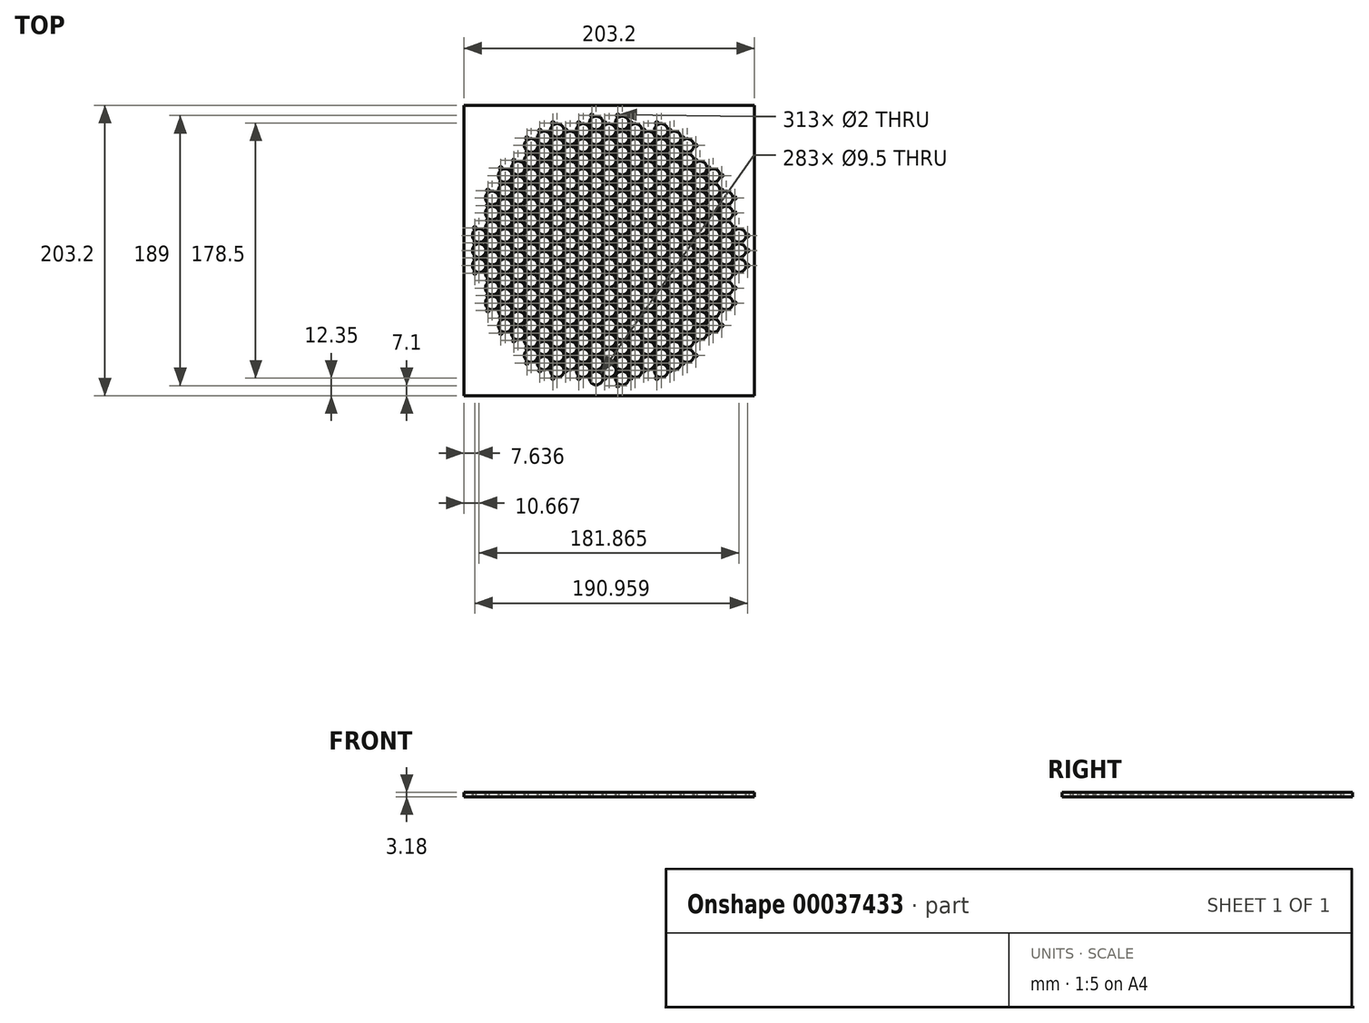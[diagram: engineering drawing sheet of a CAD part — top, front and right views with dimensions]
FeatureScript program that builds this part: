
annotation { "Feature Type Name" : "Feature", "Feature Type Description" : "" }
export const myFeature = defineFeature(function(context is Context, id is Id, definition is map)
    precondition{}
    {
        {
            var Q0;
            Q0=qCreatedBy(makeId("Top.planeOp"),FACE);
            var sketch = newSketch(context, id + "F0", { "sketchPlane" : qUnion([Q0])});
            skLineSegment(sketch, "E0.rect.bottom", {"start": v(101.6, 101.6) * mm, "end": v(-101.6, 101.6) * mm});
            skLineSegment(sketch, "E0.rect.top", {"start": v(101.6, -101.6) * mm, "end": v(-101.6, -101.6) * mm});
            skLineSegment(sketch, "E0.rect.left", {"start": v(101.6, 101.6) * mm, "end": v(101.6, -101.6) * mm});
            skLineSegment(sketch, "E0.rect.right", {"start": v(-101.6, 101.6) * mm, "end": v(-101.6, -101.6) * mm});
            skPoint(sketch, "E0.rect.middle", {"position": v(0, 0) * mm});
            skSolve(sketch);
        }
        {
            var Q0;
            Q0=qSketchRegion(id+"F0",true);
            extrude(context, id + "F1", {"entities" : qUnion([Q0]), "oppositeDirection" : true, "depth" : 3.17 * mm});
        }
        {
            var Q0;
            Q0=qCreatedBy(makeId("Top.planeOp"),FACE);
            var sketch = newSketch(context, id + "F2", { "sketchPlane" : qUnion([Q0])});
            skCircle(sketch, "E1", {"center": v(0, 0) * mm, "radius": 4.75 * mm});
            skCircle(sketch, "E2", {"center": v(0, 10.5) * mm, "radius": 4.75 * mm});
            skCircle(sketch, "E3", {"center": v(0, 21) * mm, "radius": 4.75 * mm});
            skCircle(sketch, "E4", {"center": v(0, 31.5) * mm, "radius": 4.75 * mm});
            skCircle(sketch, "E5", {"center": v(0, 42) * mm, "radius": 4.75 * mm});
            skCircle(sketch, "E6", {"center": v(0, 52.5) * mm, "radius": 4.75 * mm});
            skCircle(sketch, "E7", {"center": v(0, 63) * mm, "radius": 4.75 * mm});
            skCircle(sketch, "E8", {"center": v(0, 73.5) * mm, "radius": 4.75 * mm});
            skCircle(sketch, "E9", {"center": v(0, 84) * mm, "radius": 4.75 * mm});
            skCircle(sketch, "E10", {"center": v(0, -10.5) * mm, "radius": 4.75 * mm});
            skCircle(sketch, "E11", {"center": v(0, -21) * mm, "radius": 4.75 * mm});
            skCircle(sketch, "E12", {"center": v(0, -31.5) * mm, "radius": 4.75 * mm});
            skCircle(sketch, "E13", {"center": v(0, -42) * mm, "radius": 4.75 * mm});
            skCircle(sketch, "E14", {"center": v(0, -52.5) * mm, "radius": 4.75 * mm});
            skCircle(sketch, "E15", {"center": v(0, -63) * mm, "radius": 4.75 * mm});
            skCircle(sketch, "E16", {"center": v(0, -73.5) * mm, "radius": 4.75 * mm});
            skCircle(sketch, "E17", {"center": v(0, -84) * mm, "radius": 4.75 * mm});
            skLineSegment(sketch, "E18", {"start": v(0, 0) * mm, "end": v(9.1, 5.25) * mm, "construction": true});
            skCircle(sketch, "E19", {"center": v(9.1, -5.25) * mm, "radius": 4.75 * mm});
            skCircle(sketch, "E20", {"center": v(9.1, 26.25) * mm, "radius": 4.75 * mm});
            skCircle(sketch, "E21", {"center": v(9.1, 5.25) * mm, "radius": 4.75 * mm});
            skCircle(sketch, "E22", {"center": v(9.1, -47.25) * mm, "radius": 4.75 * mm});
            skCircle(sketch, "E23", {"center": v(9.1, 68.25) * mm, "radius": 4.75 * mm});
            skCircle(sketch, "E24", {"center": v(9.1, -36.75) * mm, "radius": 4.75 * mm});
            skCircle(sketch, "E25", {"center": v(9.1, -15.75) * mm, "radius": 4.75 * mm});
            skCircle(sketch, "E26", {"center": v(9.1, -78.75) * mm, "radius": 4.75 * mm});
            skCircle(sketch, "E27", {"center": v(9.1, -57.75) * mm, "radius": 4.75 * mm});
            skCircle(sketch, "E28", {"center": v(9.1, 89.25) * mm, "radius": 4.75 * mm});
            skCircle(sketch, "E29", {"center": v(9.1, 57.75) * mm, "radius": 4.75 * mm});
            skCircle(sketch, "E30", {"center": v(9.1, -68.25) * mm, "radius": 4.75 * mm});
            skCircle(sketch, "E31", {"center": v(9.1, 15.75) * mm, "radius": 4.75 * mm});
            skCircle(sketch, "E32", {"center": v(9.1, 47.25) * mm, "radius": 4.75 * mm});
            skCircle(sketch, "E33", {"center": v(9.1, 36.75) * mm, "radius": 4.75 * mm});
            skCircle(sketch, "E34", {"center": v(9.1, 78.75) * mm, "radius": 4.75 * mm});
            skCircle(sketch, "E35", {"center": v(9.1, -26.25) * mm, "radius": 4.75 * mm});
            skCircle(sketch, "E36", {"center": v(9.1, -89.25) * mm, "radius": 4.75 * mm});
            skCircle(sketch, "E37.1.0.0", {"center": v(18.19, 10.5) * mm, "radius": 4.75 * mm});
            skCircle(sketch, "E37.1.0.1", {"center": v(27.28, -47.25) * mm, "radius": 4.75 * mm});
            skCircle(sketch, "E37.1.0.2", {"center": v(27.28, 78.75) * mm, "radius": 4.75 * mm});
            skCircle(sketch, "E37.1.0.3", {"center": v(27.28, 57.75) * mm, "radius": 4.75 * mm});
            skCircle(sketch, "E37.1.0.4", {"center": v(18.19, -84) * mm, "radius": 4.75 * mm});
            skCircle(sketch, "E37.1.0.5", {"center": v(18.19, 52.5) * mm, "radius": 4.75 * mm});
            skCircle(sketch, "E37.1.0.6", {"center": v(27.28, 26.25) * mm, "radius": 4.75 * mm});
            skCircle(sketch, "E37.1.0.7", {"center": v(18.19, 73.5) * mm, "radius": 4.75 * mm});
            skCircle(sketch, "E37.1.0.8", {"center": v(18.19, -42) * mm, "radius": 4.75 * mm});
            skCircle(sketch, "E37.1.0.9", {"center": v(18.19, -21) * mm, "radius": 4.75 * mm});
            skCircle(sketch, "E37.1.0.10", {"center": v(18.19, -31.5) * mm, "radius": 4.75 * mm});
            skCircle(sketch, "E37.1.0.11", {"center": v(27.28, 47.25) * mm, "radius": 4.75 * mm});
            skCircle(sketch, "E37.1.0.12", {"center": v(27.28, 68.25) * mm, "radius": 4.75 * mm});
            skCircle(sketch, "E37.1.0.14", {"center": v(18.19, 31.5) * mm, "radius": 4.75 * mm});
            skCircle(sketch, "E37.1.0.15", {"center": v(18.19, 63) * mm, "radius": 4.75 * mm});
            skCircle(sketch, "E37.1.0.16", {"center": v(27.28, -26.25) * mm, "radius": 4.75 * mm});
            skCircle(sketch, "E37.1.0.17", {"center": v(18.19, -63) * mm, "radius": 4.75 * mm});
            skCircle(sketch, "E37.1.0.18", {"center": v(18.19, -10.5) * mm, "radius": 4.75 * mm});
            skCircle(sketch, "E37.1.0.19", {"center": v(27.28, 36.75) * mm, "radius": 4.75 * mm});
            skCircle(sketch, "E37.1.0.20", {"center": v(18.19, -73.5) * mm, "radius": 4.75 * mm});
            skCircle(sketch, "E37.1.0.21", {"center": v(27.28, -5.25) * mm, "radius": 4.75 * mm});
            skCircle(sketch, "E37.1.0.22", {"center": v(18.19, 21) * mm, "radius": 4.75 * mm});
            skCircle(sketch, "E37.1.0.23", {"center": v(27.28, -57.75) * mm, "radius": 4.75 * mm});
            skCircle(sketch, "E37.1.0.24", {"center": v(18.19, 84) * mm, "radius": 4.75 * mm});
            skCircle(sketch, "E37.1.0.25", {"center": v(27.28, -15.75) * mm, "radius": 4.75 * mm});
            skCircle(sketch, "E37.1.0.26", {"center": v(18.19, 42) * mm, "radius": 4.75 * mm});
            skCircle(sketch, "E37.1.0.27", {"center": v(27.28, 15.75) * mm, "radius": 4.75 * mm});
            skCircle(sketch, "E37.1.0.28", {"center": v(27.28, -68.25) * mm, "radius": 4.75 * mm});
            skCircle(sketch, "E37.1.0.29", {"center": v(27.28, -36.75) * mm, "radius": 4.75 * mm});
            skCircle(sketch, "E37.1.0.31", {"center": v(18.19, 0) * mm, "radius": 4.75 * mm});
            skCircle(sketch, "E37.1.0.32", {"center": v(27.28, -78.75) * mm, "radius": 4.75 * mm});
            skCircle(sketch, "E37.1.0.33", {"center": v(18.19, -52.5) * mm, "radius": 4.75 * mm});
            skCircle(sketch, "E37.1.0.34", {"center": v(27.28, 5.25) * mm, "radius": 4.75 * mm});
            skCircle(sketch, "E37.2.0.0", {"center": v(36.37, 10.5) * mm, "radius": 4.75 * mm});
            skCircle(sketch, "E37.2.0.1", {"center": v(45.47, -47.25) * mm, "radius": 4.75 * mm});
            skCircle(sketch, "E37.2.0.2", {"center": v(45.47, 78.75) * mm, "radius": 4.75 * mm});
            skCircle(sketch, "E37.2.0.3", {"center": v(45.47, 57.75) * mm, "radius": 4.75 * mm});
            skCircle(sketch, "E37.2.0.4", {"center": v(36.37, -84) * mm, "radius": 4.75 * mm});
            skCircle(sketch, "E37.2.0.5", {"center": v(36.37, 52.5) * mm, "radius": 4.75 * mm});
            skCircle(sketch, "E37.2.0.6", {"center": v(45.47, 26.25) * mm, "radius": 4.75 * mm});
            skCircle(sketch, "E37.2.0.7", {"center": v(36.37, 73.5) * mm, "radius": 4.75 * mm});
            skCircle(sketch, "E37.2.0.8", {"center": v(36.37, -42) * mm, "radius": 4.75 * mm});
            skCircle(sketch, "E37.2.0.9", {"center": v(36.37, -21) * mm, "radius": 4.75 * mm});
            skCircle(sketch, "E37.2.0.10", {"center": v(36.37, -31.5) * mm, "radius": 4.75 * mm});
            skCircle(sketch, "E37.2.0.11", {"center": v(45.47, 47.25) * mm, "radius": 4.75 * mm});
            skCircle(sketch, "E37.2.0.12", {"center": v(45.47, 68.25) * mm, "radius": 4.75 * mm});
            skCircle(sketch, "E37.2.0.14", {"center": v(36.37, 31.5) * mm, "radius": 4.75 * mm});
            skCircle(sketch, "E37.2.0.15", {"center": v(36.37, 63) * mm, "radius": 4.75 * mm});
            skCircle(sketch, "E37.2.0.16", {"center": v(45.47, -26.25) * mm, "radius": 4.75 * mm});
            skCircle(sketch, "E37.2.0.17", {"center": v(36.37, -63) * mm, "radius": 4.75 * mm});
            skCircle(sketch, "E37.2.0.18", {"center": v(36.37, -10.5) * mm, "radius": 4.75 * mm});
            skCircle(sketch, "E37.2.0.19", {"center": v(45.47, 36.75) * mm, "radius": 4.75 * mm});
            skCircle(sketch, "E37.2.0.20", {"center": v(36.37, -73.5) * mm, "radius": 4.75 * mm});
            skCircle(sketch, "E37.2.0.21", {"center": v(45.47, -5.25) * mm, "radius": 4.75 * mm});
            skCircle(sketch, "E37.2.0.22", {"center": v(36.37, 21) * mm, "radius": 4.75 * mm});
            skCircle(sketch, "E37.2.0.23", {"center": v(45.47, -57.75) * mm, "radius": 4.75 * mm});
            skCircle(sketch, "E37.2.0.24", {"center": v(36.37, 84) * mm, "radius": 4.75 * mm});
            skCircle(sketch, "E37.2.0.25", {"center": v(45.47, -15.75) * mm, "radius": 4.75 * mm});
            skCircle(sketch, "E37.2.0.26", {"center": v(36.37, 42) * mm, "radius": 4.75 * mm});
            skCircle(sketch, "E37.2.0.27", {"center": v(45.47, 15.75) * mm, "radius": 4.75 * mm});
            skCircle(sketch, "E37.2.0.28", {"center": v(45.47, -68.25) * mm, "radius": 4.75 * mm});
            skCircle(sketch, "E37.2.0.29", {"center": v(45.47, -36.75) * mm, "radius": 4.75 * mm});
            skCircle(sketch, "E37.2.0.31", {"center": v(36.37, 0) * mm, "radius": 4.75 * mm});
            skCircle(sketch, "E37.2.0.32", {"center": v(45.47, -78.75) * mm, "radius": 4.75 * mm});
            skCircle(sketch, "E37.2.0.33", {"center": v(36.37, -52.5) * mm, "radius": 4.75 * mm});
            skCircle(sketch, "E37.2.0.34", {"center": v(45.47, 5.25) * mm, "radius": 4.75 * mm});
            skCircle(sketch, "E37.3.0.0", {"center": v(54.56, 10.5) * mm, "radius": 4.75 * mm});
            skCircle(sketch, "E37.3.0.1", {"center": v(63.65, -47.25) * mm, "radius": 4.75 * mm});
            skCircle(sketch, "E37.3.0.3", {"center": v(63.65, 57.75) * mm, "radius": 4.75 * mm});
            skCircle(sketch, "E37.3.0.5", {"center": v(54.56, 52.5) * mm, "radius": 4.75 * mm});
            skCircle(sketch, "E37.3.0.6", {"center": v(63.65, 26.25) * mm, "radius": 4.75 * mm});
            skCircle(sketch, "E37.3.0.7", {"center": v(54.56, 73.5) * mm, "radius": 4.75 * mm});
            skCircle(sketch, "E37.3.0.8", {"center": v(54.56, -42) * mm, "radius": 4.75 * mm});
            skCircle(sketch, "E37.3.0.9", {"center": v(54.56, -21) * mm, "radius": 4.75 * mm});
            skCircle(sketch, "E37.3.0.10", {"center": v(54.56, -31.5) * mm, "radius": 4.75 * mm});
            skCircle(sketch, "E37.3.0.11", {"center": v(63.65, 47.25) * mm, "radius": 4.75 * mm});
            skCircle(sketch, "E37.3.0.14", {"center": v(54.56, 31.5) * mm, "radius": 4.75 * mm});
            skCircle(sketch, "E37.3.0.15", {"center": v(54.56, 63) * mm, "radius": 4.75 * mm});
            skCircle(sketch, "E37.3.0.16", {"center": v(63.65, -26.25) * mm, "radius": 4.75 * mm});
            skCircle(sketch, "E37.3.0.17", {"center": v(54.56, -63) * mm, "radius": 4.75 * mm});
            skCircle(sketch, "E37.3.0.18", {"center": v(54.56, -10.5) * mm, "radius": 4.75 * mm});
            skCircle(sketch, "E37.3.0.19", {"center": v(63.65, 36.75) * mm, "radius": 4.75 * mm});
            skCircle(sketch, "E37.3.0.20", {"center": v(54.56, -73.5) * mm, "radius": 4.75 * mm});
            skCircle(sketch, "E37.3.0.21", {"center": v(63.65, -5.25) * mm, "radius": 4.75 * mm});
            skCircle(sketch, "E37.3.0.22", {"center": v(54.56, 21) * mm, "radius": 4.75 * mm});
            skCircle(sketch, "E37.3.0.23", {"center": v(63.65, -57.75) * mm, "radius": 4.75 * mm});
            skCircle(sketch, "E37.3.0.25", {"center": v(63.65, -15.75) * mm, "radius": 4.75 * mm});
            skCircle(sketch, "E37.3.0.26", {"center": v(54.56, 42) * mm, "radius": 4.75 * mm});
            skCircle(sketch, "E37.3.0.27", {"center": v(63.65, 15.75) * mm, "radius": 4.75 * mm});
            skCircle(sketch, "E37.3.0.29", {"center": v(63.65, -36.75) * mm, "radius": 4.75 * mm});
            skCircle(sketch, "E37.3.0.31", {"center": v(54.56, 0) * mm, "radius": 4.75 * mm});
            skCircle(sketch, "E37.3.0.33", {"center": v(54.56, -52.5) * mm, "radius": 4.75 * mm});
            skCircle(sketch, "E37.3.0.34", {"center": v(63.65, 5.25) * mm, "radius": 4.75 * mm});
            skCircle(sketch, "E37.4.0.0", {"center": v(72.75, 10.5) * mm, "radius": 4.75 * mm});
            skCircle(sketch, "E37.4.0.5", {"center": v(72.75, 52.5) * mm, "radius": 4.75 * mm});
            skCircle(sketch, "E37.4.0.6", {"center": v(81.84, 26.25) * mm, "radius": 4.75 * mm});
            skCircle(sketch, "E37.4.0.8", {"center": v(72.75, -42) * mm, "radius": 4.75 * mm});
            skCircle(sketch, "E37.4.0.9", {"center": v(72.75, -21) * mm, "radius": 4.75 * mm});
            skCircle(sketch, "E37.4.0.10", {"center": v(72.75, -31.5) * mm, "radius": 4.75 * mm});
            skCircle(sketch, "E37.4.0.14", {"center": v(72.75, 31.5) * mm, "radius": 4.75 * mm});
            skCircle(sketch, "E37.4.0.16", {"center": v(81.84, -26.25) * mm, "radius": 4.75 * mm});
            skCircle(sketch, "E37.4.0.18", {"center": v(72.75, -10.5) * mm, "radius": 4.75 * mm});
            skCircle(sketch, "E37.4.0.19", {"center": v(81.84, 36.75) * mm, "radius": 4.75 * mm});
            skCircle(sketch, "E37.4.0.21", {"center": v(81.84, -5.25) * mm, "radius": 4.75 * mm});
            skCircle(sketch, "E37.4.0.22", {"center": v(72.75, 21) * mm, "radius": 4.75 * mm});
            skCircle(sketch, "E37.4.0.25", {"center": v(81.84, -15.75) * mm, "radius": 4.75 * mm});
            skCircle(sketch, "E37.4.0.26", {"center": v(72.75, 42) * mm, "radius": 4.75 * mm});
            skCircle(sketch, "E37.4.0.27", {"center": v(81.84, 15.75) * mm, "radius": 4.75 * mm});
            skCircle(sketch, "E37.4.0.29", {"center": v(81.84, -36.75) * mm, "radius": 4.75 * mm});
            skCircle(sketch, "E37.4.0.31", {"center": v(72.75, 0) * mm, "radius": 4.75 * mm});
            skCircle(sketch, "E37.4.0.33", {"center": v(72.75, -52.5) * mm, "radius": 4.75 * mm});
            skCircle(sketch, "E37.4.0.34", {"center": v(81.84, 5.25) * mm, "radius": 4.75 * mm});
            skCircle(sketch, "E38.1.0.0", {"center": v(-9.1, 26.25) * mm, "radius": 4.75 * mm});
            skCircle(sketch, "E38.1.0.1", {"center": v(-9.1, 5.25) * mm, "radius": 4.75 * mm});
            skCircle(sketch, "E38.1.0.2", {"center": v(-9.1, -47.25) * mm, "radius": 4.75 * mm});
            skCircle(sketch, "E38.1.0.3", {"center": v(-18.19, 84) * mm, "radius": 4.75 * mm});
            skCircle(sketch, "E38.1.0.4", {"center": v(-18.19, 31.5) * mm, "radius": 4.75 * mm});
            skCircle(sketch, "E38.1.0.5", {"center": v(-9.1, 68.25) * mm, "radius": 4.75 * mm});
            skCircle(sketch, "E38.1.0.6", {"center": v(-18.19, 42) * mm, "radius": 4.75 * mm});
            skCircle(sketch, "E38.1.0.7", {"center": v(-18.19, -10.5) * mm, "radius": 4.75 * mm});
            skCircle(sketch, "E38.1.0.8", {"center": v(-9.1, -57.75) * mm, "radius": 4.75 * mm});
            skCircle(sketch, "E38.1.0.9", {"center": v(-18.19, -42) * mm, "radius": 4.75 * mm});
            skCircle(sketch, "E38.1.0.10", {"center": v(-18.19, 63) * mm, "radius": 4.75 * mm});
            skCircle(sketch, "E38.1.0.11", {"center": v(-18.19, 0) * mm, "radius": 4.75 * mm});
            skCircle(sketch, "E38.1.0.12", {"center": v(-18.19, -21) * mm, "radius": 4.75 * mm});
            skCircle(sketch, "E38.1.0.13", {"center": v(-18.19, 21) * mm, "radius": 4.75 * mm});
            skCircle(sketch, "E38.1.0.14", {"center": v(-18.19, -63) * mm, "radius": 4.75 * mm});
            skCircle(sketch, "E38.1.0.15", {"center": v(-18.19, 52.5) * mm, "radius": 4.75 * mm});
            skCircle(sketch, "E38.1.0.16", {"center": v(-9.1, -15.75) * mm, "radius": 4.75 * mm});
            skCircle(sketch, "E38.1.0.17", {"center": v(-18.19, -73.5) * mm, "radius": 4.75 * mm});
            skCircle(sketch, "E38.1.0.18", {"center": v(-18.19, 73.5) * mm, "radius": 4.75 * mm});
            skCircle(sketch, "E38.1.0.19", {"center": v(-18.19, -31.5) * mm, "radius": 4.75 * mm});
            skCircle(sketch, "E38.1.0.20", {"center": v(-18.19, -52.5) * mm, "radius": 4.75 * mm});
            skCircle(sketch, "E38.1.0.21", {"center": v(-9.1, 89.25) * mm, "radius": 4.75 * mm});
            skCircle(sketch, "E38.1.0.22", {"center": v(-9.1, -68.25) * mm, "radius": 4.75 * mm});
            skCircle(sketch, "E38.1.0.23", {"center": v(-9.1, 57.75) * mm, "radius": 4.75 * mm});
            skCircle(sketch, "E38.1.0.24", {"center": v(-9.1, 15.75) * mm, "radius": 4.75 * mm});
            skCircle(sketch, "E38.1.0.25", {"center": v(-9.1, 47.25) * mm, "radius": 4.75 * mm});
            skLineSegment(sketch, "E38.1.0.26", {"start": v(-18.19, 10.5) * mm, "end": v(0, 10.5) * mm, "construction": true});
            skCircle(sketch, "E38.1.0.27", {"center": v(-9.1, 36.75) * mm, "radius": 4.75 * mm});
            skCircle(sketch, "E38.1.0.28", {"center": v(-18.19, -84) * mm, "radius": 4.75 * mm});
            skCircle(sketch, "E38.1.0.29", {"center": v(-9.1, 78.75) * mm, "radius": 4.75 * mm});
            skCircle(sketch, "E38.1.0.30", {"center": v(-9.1, -26.25) * mm, "radius": 4.75 * mm});
            skCircle(sketch, "E38.1.0.31", {"center": v(-9.1, -5.25) * mm, "radius": 4.75 * mm});
            skCircle(sketch, "E38.1.0.32", {"center": v(-9.1, -89.25) * mm, "radius": 4.75 * mm});
            skCircle(sketch, "E38.1.0.33", {"center": v(-18.19, 10.5) * mm, "radius": 4.75 * mm});
            skCircle(sketch, "E38.1.0.34", {"center": v(-9.1, -36.75) * mm, "radius": 4.75 * mm});
            skCircle(sketch, "E38.1.0.35", {"center": v(-9.1, -78.75) * mm, "radius": 4.75 * mm});
            skLineSegment(sketch, "E38.1.0.36", {"start": v(-18.19, 0) * mm, "end": v(-9.1, 5.25) * mm, "construction": true});
            skCircle(sketch, "E38.2.0.0", {"center": v(-27.28, 26.25) * mm, "radius": 4.75 * mm});
            skCircle(sketch, "E38.2.0.1", {"center": v(-27.28, 5.25) * mm, "radius": 4.75 * mm});
            skCircle(sketch, "E38.2.0.2", {"center": v(-27.28, -47.25) * mm, "radius": 4.75 * mm});
            skCircle(sketch, "E38.2.0.3", {"center": v(-36.37, 84) * mm, "radius": 4.75 * mm});
            skCircle(sketch, "E38.2.0.4", {"center": v(-36.37, 31.5) * mm, "radius": 4.75 * mm});
            skCircle(sketch, "E38.2.0.5", {"center": v(-27.28, 68.25) * mm, "radius": 4.75 * mm});
            skCircle(sketch, "E38.2.0.6", {"center": v(-36.37, 42) * mm, "radius": 4.75 * mm});
            skCircle(sketch, "E38.2.0.7", {"center": v(-36.37, -10.5) * mm, "radius": 4.75 * mm});
            skCircle(sketch, "E38.2.0.8", {"center": v(-27.28, -57.75) * mm, "radius": 4.75 * mm});
            skCircle(sketch, "E38.2.0.9", {"center": v(-36.37, -42) * mm, "radius": 4.75 * mm});
            skCircle(sketch, "E38.2.0.10", {"center": v(-36.37, 63) * mm, "radius": 4.75 * mm});
            skCircle(sketch, "E38.2.0.11", {"center": v(-36.37, 0) * mm, "radius": 4.75 * mm});
            skCircle(sketch, "E38.2.0.12", {"center": v(-36.37, -21) * mm, "radius": 4.75 * mm});
            skCircle(sketch, "E38.2.0.13", {"center": v(-36.37, 21) * mm, "radius": 4.75 * mm});
            skCircle(sketch, "E38.2.0.14", {"center": v(-36.37, -63) * mm, "radius": 4.75 * mm});
            skCircle(sketch, "E38.2.0.15", {"center": v(-36.37, 52.5) * mm, "radius": 4.75 * mm});
            skCircle(sketch, "E38.2.0.16", {"center": v(-27.28, -15.75) * mm, "radius": 4.75 * mm});
            skCircle(sketch, "E38.2.0.17", {"center": v(-36.37, -73.5) * mm, "radius": 4.75 * mm});
            skCircle(sketch, "E38.2.0.18", {"center": v(-36.37, 73.5) * mm, "radius": 4.75 * mm});
            skCircle(sketch, "E38.2.0.19", {"center": v(-36.37, -31.5) * mm, "radius": 4.75 * mm});
            skCircle(sketch, "E38.2.0.20", {"center": v(-36.37, -52.5) * mm, "radius": 4.75 * mm});
            skCircle(sketch, "E38.2.0.22", {"center": v(-27.28, -68.25) * mm, "radius": 4.75 * mm});
            skCircle(sketch, "E38.2.0.23", {"center": v(-27.28, 57.75) * mm, "radius": 4.75 * mm});
            skCircle(sketch, "E38.2.0.24", {"center": v(-27.28, 15.75) * mm, "radius": 4.75 * mm});
            skCircle(sketch, "E38.2.0.25", {"center": v(-27.28, 47.25) * mm, "radius": 4.75 * mm});
            skLineSegment(sketch, "E38.2.0.26", {"start": v(-36.37, 10.5) * mm, "end": v(-18.19, 10.5) * mm, "construction": true});
            skCircle(sketch, "E38.2.0.27", {"center": v(-27.28, 36.75) * mm, "radius": 4.75 * mm});
            skCircle(sketch, "E38.2.0.28", {"center": v(-36.37, -84) * mm, "radius": 4.75 * mm});
            skCircle(sketch, "E38.2.0.29", {"center": v(-27.28, 78.75) * mm, "radius": 4.75 * mm});
            skCircle(sketch, "E38.2.0.30", {"center": v(-27.28, -26.25) * mm, "radius": 4.75 * mm});
            skCircle(sketch, "E38.2.0.31", {"center": v(-27.28, -5.25) * mm, "radius": 4.75 * mm});
            skCircle(sketch, "E38.2.0.33", {"center": v(-36.37, 10.5) * mm, "radius": 4.75 * mm});
            skCircle(sketch, "E38.2.0.34", {"center": v(-27.28, -36.75) * mm, "radius": 4.75 * mm});
            skCircle(sketch, "E38.2.0.35", {"center": v(-27.28, -78.75) * mm, "radius": 4.75 * mm});
            skLineSegment(sketch, "E38.2.0.36", {"start": v(-36.37, 0) * mm, "end": v(-27.28, 5.25) * mm, "construction": true});
            skCircle(sketch, "E38.3.0.0", {"center": v(-45.47, 26.25) * mm, "radius": 4.75 * mm});
            skCircle(sketch, "E38.3.0.1", {"center": v(-45.47, 5.25) * mm, "radius": 4.75 * mm});
            skCircle(sketch, "E38.3.0.2", {"center": v(-45.47, -47.25) * mm, "radius": 4.75 * mm});
            skCircle(sketch, "E38.3.0.4", {"center": v(-54.56, 31.5) * mm, "radius": 4.75 * mm});
            skCircle(sketch, "E38.3.0.5", {"center": v(-45.47, 68.25) * mm, "radius": 4.75 * mm});
            skCircle(sketch, "E38.3.0.6", {"center": v(-54.56, 42) * mm, "radius": 4.75 * mm});
            skCircle(sketch, "E38.3.0.7", {"center": v(-54.56, -10.5) * mm, "radius": 4.75 * mm});
            skCircle(sketch, "E38.3.0.8", {"center": v(-45.47, -57.75) * mm, "radius": 4.75 * mm});
            skCircle(sketch, "E38.3.0.9", {"center": v(-54.56, -42) * mm, "radius": 4.75 * mm});
            skCircle(sketch, "E38.3.0.10", {"center": v(-54.56, 63) * mm, "radius": 4.75 * mm});
            skCircle(sketch, "E38.3.0.11", {"center": v(-54.56, 0) * mm, "radius": 4.75 * mm});
            skCircle(sketch, "E38.3.0.12", {"center": v(-54.56, -21) * mm, "radius": 4.75 * mm});
            skCircle(sketch, "E38.3.0.13", {"center": v(-54.56, 21) * mm, "radius": 4.75 * mm});
            skCircle(sketch, "E38.3.0.14", {"center": v(-54.56, -63) * mm, "radius": 4.75 * mm});
            skCircle(sketch, "E38.3.0.15", {"center": v(-54.56, 52.5) * mm, "radius": 4.75 * mm});
            skCircle(sketch, "E38.3.0.16", {"center": v(-45.47, -15.75) * mm, "radius": 4.75 * mm});
            skCircle(sketch, "E38.3.0.17", {"center": v(-54.56, -73.5) * mm, "radius": 4.75 * mm});
            skCircle(sketch, "E38.3.0.18", {"center": v(-54.56, 73.5) * mm, "radius": 4.75 * mm});
            skCircle(sketch, "E38.3.0.19", {"center": v(-54.56, -31.5) * mm, "radius": 4.75 * mm});
            skCircle(sketch, "E38.3.0.20", {"center": v(-54.56, -52.5) * mm, "radius": 4.75 * mm});
            skCircle(sketch, "E38.3.0.22", {"center": v(-45.47, -68.25) * mm, "radius": 4.75 * mm});
            skCircle(sketch, "E38.3.0.23", {"center": v(-45.47, 57.75) * mm, "radius": 4.75 * mm});
            skCircle(sketch, "E38.3.0.24", {"center": v(-45.47, 15.75) * mm, "radius": 4.75 * mm});
            skCircle(sketch, "E38.3.0.25", {"center": v(-45.47, 47.25) * mm, "radius": 4.75 * mm});
            skLineSegment(sketch, "E38.3.0.26", {"start": v(-54.56, 10.5) * mm, "end": v(-36.37, 10.5) * mm, "construction": true});
            skCircle(sketch, "E38.3.0.27", {"center": v(-45.47, 36.75) * mm, "radius": 4.75 * mm});
            skCircle(sketch, "E38.3.0.29", {"center": v(-45.47, 78.75) * mm, "radius": 4.75 * mm});
            skCircle(sketch, "E38.3.0.30", {"center": v(-45.47, -26.25) * mm, "radius": 4.75 * mm});
            skCircle(sketch, "E38.3.0.31", {"center": v(-45.47, -5.25) * mm, "radius": 4.75 * mm});
            skCircle(sketch, "E38.3.0.33", {"center": v(-54.56, 10.5) * mm, "radius": 4.75 * mm});
            skCircle(sketch, "E38.3.0.34", {"center": v(-45.47, -36.75) * mm, "radius": 4.75 * mm});
            skCircle(sketch, "E38.3.0.35", {"center": v(-45.47, -78.75) * mm, "radius": 4.75 * mm});
            skLineSegment(sketch, "E38.3.0.36", {"start": v(-54.56, 0) * mm, "end": v(-45.47, 5.25) * mm, "construction": true});
            skCircle(sketch, "E38.4.0.0", {"center": v(-63.65, 26.25) * mm, "radius": 4.75 * mm});
            skCircle(sketch, "E38.4.0.1", {"center": v(-63.65, 5.25) * mm, "radius": 4.75 * mm});
            skCircle(sketch, "E38.4.0.2", {"center": v(-63.65, -47.25) * mm, "radius": 4.75 * mm});
            skCircle(sketch, "E38.4.0.4", {"center": v(-72.75, 31.5) * mm, "radius": 4.75 * mm});
            skCircle(sketch, "E38.4.0.6", {"center": v(-72.75, 42) * mm, "radius": 4.75 * mm});
            skCircle(sketch, "E38.4.0.7", {"center": v(-72.75, -10.5) * mm, "radius": 4.75 * mm});
            skCircle(sketch, "E38.4.0.8", {"center": v(-63.65, -57.75) * mm, "radius": 4.75 * mm});
            skCircle(sketch, "E38.4.0.9", {"center": v(-72.75, -42) * mm, "radius": 4.75 * mm});
            skCircle(sketch, "E38.4.0.11", {"center": v(-72.75, 0) * mm, "radius": 4.75 * mm});
            skCircle(sketch, "E38.4.0.12", {"center": v(-72.75, -21) * mm, "radius": 4.75 * mm});
            skCircle(sketch, "E38.4.0.13", {"center": v(-72.75, 21) * mm, "radius": 4.75 * mm});
            skCircle(sketch, "E38.4.0.15", {"center": v(-72.75, 52.5) * mm, "radius": 4.75 * mm});
            skCircle(sketch, "E38.4.0.16", {"center": v(-63.65, -15.75) * mm, "radius": 4.75 * mm});
            skCircle(sketch, "E38.4.0.19", {"center": v(-72.75, -31.5) * mm, "radius": 4.75 * mm});
            skCircle(sketch, "E38.4.0.20", {"center": v(-72.75, -52.5) * mm, "radius": 4.75 * mm});
            skCircle(sketch, "E38.4.0.23", {"center": v(-63.65, 57.75) * mm, "radius": 4.75 * mm});
            skCircle(sketch, "E38.4.0.24", {"center": v(-63.65, 15.75) * mm, "radius": 4.75 * mm});
            skCircle(sketch, "E38.4.0.25", {"center": v(-63.65, 47.25) * mm, "radius": 4.75 * mm});
            skLineSegment(sketch, "E38.4.0.26", {"start": v(-72.75, 10.5) * mm, "end": v(-54.56, 10.5) * mm, "construction": true});
            skCircle(sketch, "E38.4.0.27", {"center": v(-63.65, 36.75) * mm, "radius": 4.75 * mm});
            skCircle(sketch, "E38.4.0.30", {"center": v(-63.65, -26.25) * mm, "radius": 4.75 * mm});
            skCircle(sketch, "E38.4.0.31", {"center": v(-63.65, -5.25) * mm, "radius": 4.75 * mm});
            skCircle(sketch, "E38.4.0.33", {"center": v(-72.75, 10.5) * mm, "radius": 4.75 * mm});
            skCircle(sketch, "E38.4.0.34", {"center": v(-63.65, -36.75) * mm, "radius": 4.75 * mm});
            skLineSegment(sketch, "E38.4.0.36", {"start": v(-72.75, 0) * mm, "end": v(-63.65, 5.25) * mm, "construction": true});
            skCircle(sketch, "E39", {"center": v(0, 0) * mm, "radius": 100 * mm, "construction": true});
            skCircle(sketch, "E40.1.0.0", {"center": v(-81.84, -26.25) * mm, "radius": 4.75 * mm});
            skCircle(sketch, "E40.1.0.8", {"center": v(-81.84, -5.25) * mm, "radius": 4.75 * mm});
            skCircle(sketch, "E40.1.0.13", {"center": v(-90.93, 0) * mm, "radius": 4.75 * mm});
            skCircle(sketch, "E40.1.0.14", {"center": v(-81.84, 36.75) * mm, "radius": 4.75 * mm});
            skCircle(sketch, "E40.1.0.19", {"center": v(-81.84, -36.75) * mm, "radius": 4.75 * mm});
            skCircle(sketch, "E40.1.0.22", {"center": v(-81.84, 15.75) * mm, "radius": 4.75 * mm});
            skCircle(sketch, "E40.1.0.25", {"center": v(-90.93, 10.5) * mm, "radius": 4.75 * mm});
            skCircle(sketch, "E40.1.0.26", {"center": v(-81.84, 5.25) * mm, "radius": 4.75 * mm});
            skCircle(sketch, "E40.1.0.28", {"center": v(-90.93, -10.5) * mm, "radius": 4.75 * mm});
            skCircle(sketch, "E40.1.0.29", {"center": v(-81.84, -15.75) * mm, "radius": 4.75 * mm});
            skCircle(sketch, "E40.1.0.31", {"center": v(-81.84, 26.25) * mm, "radius": 4.75 * mm});
            skLineSegment(sketch, "E40.1.0.35", {"start": v(-90.93, 0) * mm, "end": v(-81.84, 5.25) * mm, "construction": true});
            skLineSegment(sketch, "E40.direction1", {"start": v(-63.65, -26.25) * mm, "end": v(-81.84, -26.25) * mm, "construction": true});
            skCircle(sketch, "E41.1.0.3", {"center": v(90.93, 10.5) * mm, "radius": 4.75 * mm});
            skCircle(sketch, "E41.1.0.13", {"center": v(90.93, -10.5) * mm, "radius": 4.75 * mm});
            skCircle(sketch, "E41.1.0.30", {"center": v(90.93, 0) * mm, "radius": 4.75 * mm});
            skSolve(sketch);
        }
        {
            var Q0;
            Q0=qCreatedBy(makeId("Top.planeOp"),FACE);
            var sketch = newSketch(context, id + "F3", { "sketchPlane" : qUnion([Q0])});
            skCircle(sketch, "E42", {"center": v(6.06, 0) * mm, "radius": 1 * mm});
            skCircle(sketch, "E43.1.0", {"center": v(-3.03, 5.25) * mm, "radius": 1 * mm});
            skCircle(sketch, "E43.2.0", {"center": v(-3.03, -5.25) * mm, "radius": 1 * mm});
            skPoint(sketch, "E43.center", {"position": v(0, 0) * mm});
            skCircle(sketch, "E44.1.0.0", {"center": v(15.16, 5.25) * mm, "radius": 1 * mm});
            skCircle(sketch, "E44.1.0.1", {"center": v(24.25, 0) * mm, "radius": 1 * mm});
            skCircle(sketch, "E44.1.0.2", {"center": v(15.16, -5.25) * mm, "radius": 1 * mm});
            skCircle(sketch, "E44.2.0.0", {"center": v(33.34, 5.25) * mm, "radius": 1 * mm});
            skCircle(sketch, "E44.2.0.1", {"center": v(42.44, 0) * mm, "radius": 1 * mm});
            skCircle(sketch, "E44.2.0.2", {"center": v(33.34, -5.25) * mm, "radius": 1 * mm});
            skCircle(sketch, "E44.3.0.0", {"center": v(51.53, 5.25) * mm, "radius": 1 * mm});
            skCircle(sketch, "E44.3.0.1", {"center": v(60.62, 0) * mm, "radius": 1 * mm});
            skCircle(sketch, "E44.3.0.2", {"center": v(51.53, -5.25) * mm, "radius": 1 * mm});
            skCircle(sketch, "E44.4.0.0", {"center": v(69.72, 5.25) * mm, "radius": 1 * mm});
            skCircle(sketch, "E44.4.0.1", {"center": v(78.8, 0) * mm, "radius": 1 * mm});
            skCircle(sketch, "E44.4.0.2", {"center": v(69.72, -5.25) * mm, "radius": 1 * mm});
            skCircle(sketch, "E44.5.0.0", {"center": v(87.9, 5.25) * mm, "radius": 1 * mm});
            skCircle(sketch, "E44.5.0.1", {"center": v(97, 0) * mm, "radius": 1 * mm});
            skCircle(sketch, "E44.5.0.2", {"center": v(87.9, -5.25) * mm, "radius": 1 * mm});
            skCircle(sketch, "E45.1.0.0", {"center": v(-12.12, 0) * mm, "radius": 1 * mm});
            skCircle(sketch, "E45.1.0.1", {"center": v(-21.22, -5.25) * mm, "radius": 1 * mm});
            skCircle(sketch, "E45.1.0.2", {"center": v(-21.22, 5.25) * mm, "radius": 1 * mm});
            skCircle(sketch, "E45.2.0.0", {"center": v(-30.31, 0) * mm, "radius": 1 * mm});
            skCircle(sketch, "E45.2.0.1", {"center": v(-39.4, -5.25) * mm, "radius": 1 * mm});
            skCircle(sketch, "E45.2.0.2", {"center": v(-39.4, 5.25) * mm, "radius": 1 * mm});
            skCircle(sketch, "E45.3.0.0", {"center": v(-48.5, 0) * mm, "radius": 1 * mm});
            skCircle(sketch, "E45.3.0.1", {"center": v(-57.6, -5.25) * mm, "radius": 1 * mm});
            skCircle(sketch, "E45.3.0.2", {"center": v(-57.6, 5.25) * mm, "radius": 1 * mm});
            skCircle(sketch, "E45.4.0.0", {"center": v(-66.68, 0) * mm, "radius": 1 * mm});
            skCircle(sketch, "E45.4.0.1", {"center": v(-75.78, -5.25) * mm, "radius": 1 * mm});
            skCircle(sketch, "E45.4.0.2", {"center": v(-75.78, 5.25) * mm, "radius": 1 * mm});
            skCircle(sketch, "E45.5.0.0", {"center": v(-84.87, 0) * mm, "radius": 1 * mm});
            skCircle(sketch, "E45.5.0.1", {"center": v(-93.96, -5.25) * mm, "radius": 1 * mm});
            skCircle(sketch, "E45.5.0.2", {"center": v(-93.96, 5.25) * mm, "radius": 1 * mm});
            skPoint(sketch, "E46.0.1.1", {"position": v(0, 10.5) * mm});
            skCircle(sketch, "E46.0.1.6", {"center": v(-48.5, 10.5) * mm, "radius": 1 * mm});
            skCircle(sketch, "E46.0.1.8", {"center": v(51.53, 15.75) * mm, "radius": 1 * mm});
            skCircle(sketch, "E46.0.1.10", {"center": v(42.44, 10.5) * mm, "radius": 1 * mm});
            skCircle(sketch, "E46.0.1.11", {"center": v(33.34, 15.75) * mm, "radius": 1 * mm});
            skCircle(sketch, "E46.0.1.12", {"center": v(24.25, 10.5) * mm, "radius": 1 * mm});
            skCircle(sketch, "E46.0.1.13", {"center": v(-57.6, 15.75) * mm, "radius": 1 * mm});
            skCircle(sketch, "E46.0.1.15", {"center": v(-39.4, 15.75) * mm, "radius": 1 * mm});
            skCircle(sketch, "E46.0.1.17", {"center": v(87.9, 15.75) * mm, "radius": 1 * mm});
            skCircle(sketch, "E46.0.1.18", {"center": v(60.62, 10.5) * mm, "radius": 1 * mm});
            skCircle(sketch, "E46.0.1.19", {"center": v(-66.68, 10.5) * mm, "radius": 1 * mm});
            skCircle(sketch, "E46.0.1.20", {"center": v(-30.31, 10.5) * mm, "radius": 1 * mm});
            skCircle(sketch, "E46.0.1.21", {"center": v(-75.78, 15.75) * mm, "radius": 1 * mm});
            skCircle(sketch, "E46.0.1.23", {"center": v(-93.96, 15.75) * mm, "radius": 1 * mm});
            skCircle(sketch, "E46.0.1.27", {"center": v(97, 10.5) * mm, "radius": 1 * mm});
            skCircle(sketch, "E46.0.1.29", {"center": v(78.8, 10.5) * mm, "radius": 1 * mm});
            skCircle(sketch, "E46.0.1.30", {"center": v(69.72, 15.75) * mm, "radius": 1 * mm});
            skCircle(sketch, "E46.0.1.31", {"center": v(-84.87, 10.5) * mm, "radius": 1 * mm});
            skCircle(sketch, "E46.0.1.33", {"center": v(-21.22, 15.75) * mm, "radius": 1 * mm});
            skCircle(sketch, "E46.0.1.34", {"center": v(6.06, 10.5) * mm, "radius": 1 * mm});
            skCircle(sketch, "E46.0.1.35", {"center": v(-12.12, 10.5) * mm, "radius": 1 * mm});
            skCircle(sketch, "E46.0.1.36", {"center": v(15.16, 15.75) * mm, "radius": 1 * mm});
            skCircle(sketch, "E46.0.1.37", {"center": v(-3.03, 15.75) * mm, "radius": 1 * mm});
            skPoint(sketch, "E46.0.2.1", {"position": v(0, 21) * mm});
            skCircle(sketch, "E46.0.2.5", {"center": v(87.9, 15.75) * mm, "radius": 1 * mm});
            skCircle(sketch, "E46.0.2.6", {"center": v(-48.5, 21) * mm, "radius": 1 * mm});
            skCircle(sketch, "E46.0.2.7", {"center": v(-39.4, 15.75) * mm, "radius": 1 * mm});
            skCircle(sketch, "E46.0.2.8", {"center": v(51.53, 26.25) * mm, "radius": 1 * mm});
            skCircle(sketch, "E46.0.2.9", {"center": v(33.34, 15.75) * mm, "radius": 1 * mm});
            skCircle(sketch, "E46.0.2.10", {"center": v(42.44, 21) * mm, "radius": 1 * mm});
            skCircle(sketch, "E46.0.2.11", {"center": v(33.34, 26.25) * mm, "radius": 1 * mm});
            skCircle(sketch, "E46.0.2.12", {"center": v(24.25, 21) * mm, "radius": 1 * mm});
            skCircle(sketch, "E46.0.2.13", {"center": v(-57.6, 26.25) * mm, "radius": 1 * mm});
            skCircle(sketch, "E46.0.2.14", {"center": v(-75.78, 15.75) * mm, "radius": 1 * mm});
            skCircle(sketch, "E46.0.2.15", {"center": v(-39.4, 26.25) * mm, "radius": 1 * mm});
            skCircle(sketch, "E46.0.2.16", {"center": v(69.72, 15.75) * mm, "radius": 1 * mm});
            skCircle(sketch, "E46.0.2.17", {"center": v(87.9, 26.25) * mm, "radius": 1 * mm});
            skCircle(sketch, "E46.0.2.18", {"center": v(60.62, 21) * mm, "radius": 1 * mm});
            skCircle(sketch, "E46.0.2.19", {"center": v(-66.68, 21) * mm, "radius": 1 * mm});
            skCircle(sketch, "E46.0.2.20", {"center": v(-30.31, 21) * mm, "radius": 1 * mm});
            skCircle(sketch, "E46.0.2.21", {"center": v(-75.78, 26.25) * mm, "radius": 1 * mm});
            skCircle(sketch, "E46.0.2.22", {"center": v(-57.6, 15.75) * mm, "radius": 1 * mm});
            skCircle(sketch, "E46.0.2.24", {"center": v(-3.03, 15.75) * mm, "radius": 1 * mm});
            skCircle(sketch, "E46.0.2.25", {"center": v(15.16, 15.75) * mm, "radius": 1 * mm});
            skCircle(sketch, "E46.0.2.26", {"center": v(51.53, 15.75) * mm, "radius": 1 * mm});
            skCircle(sketch, "E46.0.2.28", {"center": v(-93.96, 15.75) * mm, "radius": 1 * mm});
            skCircle(sketch, "E46.0.2.29", {"center": v(78.8, 21) * mm, "radius": 1 * mm});
            skCircle(sketch, "E46.0.2.30", {"center": v(69.72, 26.25) * mm, "radius": 1 * mm});
            skCircle(sketch, "E46.0.2.31", {"center": v(-84.87, 21) * mm, "radius": 1 * mm});
            skCircle(sketch, "E46.0.2.32", {"center": v(-21.22, 15.75) * mm, "radius": 1 * mm});
            skCircle(sketch, "E46.0.2.33", {"center": v(-21.22, 26.25) * mm, "radius": 1 * mm});
            skCircle(sketch, "E46.0.2.34", {"center": v(6.06, 21) * mm, "radius": 1 * mm});
            skCircle(sketch, "E46.0.2.35", {"center": v(-12.12, 21) * mm, "radius": 1 * mm});
            skCircle(sketch, "E46.0.2.36", {"center": v(15.16, 26.25) * mm, "radius": 1 * mm});
            skCircle(sketch, "E46.0.2.37", {"center": v(-3.03, 26.25) * mm, "radius": 1 * mm});
            skPoint(sketch, "E46.0.3.1", {"position": v(0, 31.5) * mm});
            skCircle(sketch, "E46.0.3.5", {"center": v(87.9, 26.25) * mm, "radius": 1 * mm});
            skCircle(sketch, "E46.0.3.6", {"center": v(-48.5, 31.5) * mm, "radius": 1 * mm});
            skCircle(sketch, "E46.0.3.7", {"center": v(-39.4, 26.25) * mm, "radius": 1 * mm});
            skCircle(sketch, "E46.0.3.8", {"center": v(51.53, 36.75) * mm, "radius": 1 * mm});
            skCircle(sketch, "E46.0.3.9", {"center": v(33.34, 26.25) * mm, "radius": 1 * mm});
            skCircle(sketch, "E46.0.3.10", {"center": v(42.44, 31.5) * mm, "radius": 1 * mm});
            skCircle(sketch, "E46.0.3.11", {"center": v(33.34, 36.75) * mm, "radius": 1 * mm});
            skCircle(sketch, "E46.0.3.12", {"center": v(24.25, 31.5) * mm, "radius": 1 * mm});
            skCircle(sketch, "E46.0.3.13", {"center": v(-57.6, 36.75) * mm, "radius": 1 * mm});
            skCircle(sketch, "E46.0.3.14", {"center": v(-75.78, 26.25) * mm, "radius": 1 * mm});
            skCircle(sketch, "E46.0.3.15", {"center": v(-39.4, 36.75) * mm, "radius": 1 * mm});
            skCircle(sketch, "E46.0.3.16", {"center": v(69.72, 26.25) * mm, "radius": 1 * mm});
            skCircle(sketch, "E46.0.3.17", {"center": v(87.9, 36.75) * mm, "radius": 1 * mm});
            skCircle(sketch, "E46.0.3.18", {"center": v(60.62, 31.5) * mm, "radius": 1 * mm});
            skCircle(sketch, "E46.0.3.19", {"center": v(-66.68, 31.5) * mm, "radius": 1 * mm});
            skCircle(sketch, "E46.0.3.20", {"center": v(-30.31, 31.5) * mm, "radius": 1 * mm});
            skCircle(sketch, "E46.0.3.21", {"center": v(-75.78, 36.75) * mm, "radius": 1 * mm});
            skCircle(sketch, "E46.0.3.22", {"center": v(-57.6, 26.25) * mm, "radius": 1 * mm});
            skCircle(sketch, "E46.0.3.24", {"center": v(-3.03, 26.25) * mm, "radius": 1 * mm});
            skCircle(sketch, "E46.0.3.25", {"center": v(15.16, 26.25) * mm, "radius": 1 * mm});
            skCircle(sketch, "E46.0.3.26", {"center": v(51.53, 26.25) * mm, "radius": 1 * mm});
            skCircle(sketch, "E46.0.3.29", {"center": v(78.8, 31.5) * mm, "radius": 1 * mm});
            skCircle(sketch, "E46.0.3.30", {"center": v(69.72, 36.75) * mm, "radius": 1 * mm});
            skCircle(sketch, "E46.0.3.31", {"center": v(-84.87, 31.5) * mm, "radius": 1 * mm});
            skCircle(sketch, "E46.0.3.32", {"center": v(-21.22, 26.25) * mm, "radius": 1 * mm});
            skCircle(sketch, "E46.0.3.33", {"center": v(-21.22, 36.75) * mm, "radius": 1 * mm});
            skCircle(sketch, "E46.0.3.34", {"center": v(6.06, 31.5) * mm, "radius": 1 * mm});
            skCircle(sketch, "E46.0.3.35", {"center": v(-12.12, 31.5) * mm, "radius": 1 * mm});
            skCircle(sketch, "E46.0.3.36", {"center": v(15.16, 36.75) * mm, "radius": 1 * mm});
            skCircle(sketch, "E46.0.3.37", {"center": v(-3.03, 36.75) * mm, "radius": 1 * mm});
            skPoint(sketch, "E46.0.4.1", {"position": v(0, 42) * mm});
            skCircle(sketch, "E46.0.4.5", {"center": v(87.9, 36.75) * mm, "radius": 1 * mm});
            skCircle(sketch, "E46.0.4.6", {"center": v(-48.5, 42) * mm, "radius": 1 * mm});
            skCircle(sketch, "E46.0.4.7", {"center": v(-39.4, 36.75) * mm, "radius": 1 * mm});
            skCircle(sketch, "E46.0.4.8", {"center": v(51.53, 47.25) * mm, "radius": 1 * mm});
            skCircle(sketch, "E46.0.4.9", {"center": v(33.34, 36.75) * mm, "radius": 1 * mm});
            skCircle(sketch, "E46.0.4.10", {"center": v(42.44, 42) * mm, "radius": 1 * mm});
            skCircle(sketch, "E46.0.4.11", {"center": v(33.34, 47.25) * mm, "radius": 1 * mm});
            skCircle(sketch, "E46.0.4.12", {"center": v(24.25, 42) * mm, "radius": 1 * mm});
            skCircle(sketch, "E46.0.4.13", {"center": v(-57.6, 47.25) * mm, "radius": 1 * mm});
            skCircle(sketch, "E46.0.4.14", {"center": v(-75.78, 36.75) * mm, "radius": 1 * mm});
            skCircle(sketch, "E46.0.4.15", {"center": v(-39.4, 47.25) * mm, "radius": 1 * mm});
            skCircle(sketch, "E46.0.4.16", {"center": v(69.72, 36.75) * mm, "radius": 1 * mm});
            skCircle(sketch, "E46.0.4.18", {"center": v(60.62, 42) * mm, "radius": 1 * mm});
            skCircle(sketch, "E46.0.4.19", {"center": v(-66.68, 42) * mm, "radius": 1 * mm});
            skCircle(sketch, "E46.0.4.20", {"center": v(-30.31, 42) * mm, "radius": 1 * mm});
            skCircle(sketch, "E46.0.4.21", {"center": v(-75.78, 47.25) * mm, "radius": 1 * mm});
            skCircle(sketch, "E46.0.4.22", {"center": v(-57.6, 36.75) * mm, "radius": 1 * mm});
            skCircle(sketch, "E46.0.4.24", {"center": v(-3.03, 36.75) * mm, "radius": 1 * mm});
            skCircle(sketch, "E46.0.4.25", {"center": v(15.16, 36.75) * mm, "radius": 1 * mm});
            skCircle(sketch, "E46.0.4.26", {"center": v(51.53, 36.75) * mm, "radius": 1 * mm});
            skCircle(sketch, "E46.0.4.29", {"center": v(78.8, 42) * mm, "radius": 1 * mm});
            skCircle(sketch, "E46.0.4.30", {"center": v(69.72, 47.25) * mm, "radius": 1 * mm});
            skCircle(sketch, "E46.0.4.31", {"center": v(-84.87, 42) * mm, "radius": 1 * mm});
            skCircle(sketch, "E46.0.4.32", {"center": v(-21.22, 36.75) * mm, "radius": 1 * mm});
            skCircle(sketch, "E46.0.4.33", {"center": v(-21.22, 47.25) * mm, "radius": 1 * mm});
            skCircle(sketch, "E46.0.4.34", {"center": v(6.06, 42) * mm, "radius": 1 * mm});
            skCircle(sketch, "E46.0.4.35", {"center": v(-12.12, 42) * mm, "radius": 1 * mm});
            skCircle(sketch, "E46.0.4.36", {"center": v(15.16, 47.25) * mm, "radius": 1 * mm});
            skCircle(sketch, "E46.0.4.37", {"center": v(-3.03, 47.25) * mm, "radius": 1 * mm});
            skPoint(sketch, "E46.0.5.1", {"position": v(0, 52.5) * mm});
            skCircle(sketch, "E46.0.5.6", {"center": v(-48.5, 52.5) * mm, "radius": 1 * mm});
            skCircle(sketch, "E46.0.5.7", {"center": v(-39.4, 47.25) * mm, "radius": 1 * mm});
            skCircle(sketch, "E46.0.5.8", {"center": v(51.53, 57.75) * mm, "radius": 1 * mm});
            skCircle(sketch, "E46.0.5.9", {"center": v(33.34, 47.25) * mm, "radius": 1 * mm});
            skCircle(sketch, "E46.0.5.10", {"center": v(42.44, 52.5) * mm, "radius": 1 * mm});
            skCircle(sketch, "E46.0.5.11", {"center": v(33.34, 57.75) * mm, "radius": 1 * mm});
            skCircle(sketch, "E46.0.5.12", {"center": v(24.25, 52.5) * mm, "radius": 1 * mm});
            skCircle(sketch, "E46.0.5.13", {"center": v(-57.6, 57.75) * mm, "radius": 1 * mm});
            skCircle(sketch, "E46.0.5.14", {"center": v(-75.78, 47.25) * mm, "radius": 1 * mm});
            skCircle(sketch, "E46.0.5.15", {"center": v(-39.4, 57.75) * mm, "radius": 1 * mm});
            skCircle(sketch, "E46.0.5.16", {"center": v(69.72, 47.25) * mm, "radius": 1 * mm});
            skCircle(sketch, "E46.0.5.18", {"center": v(60.62, 52.5) * mm, "radius": 1 * mm});
            skCircle(sketch, "E46.0.5.19", {"center": v(-66.68, 52.5) * mm, "radius": 1 * mm});
            skCircle(sketch, "E46.0.5.20", {"center": v(-30.31, 52.5) * mm, "radius": 1 * mm});
            skCircle(sketch, "E46.0.5.21", {"center": v(-75.78, 57.75) * mm, "radius": 1 * mm});
            skCircle(sketch, "E46.0.5.22", {"center": v(-57.6, 47.25) * mm, "radius": 1 * mm});
            skCircle(sketch, "E46.0.5.24", {"center": v(-3.03, 47.25) * mm, "radius": 1 * mm});
            skCircle(sketch, "E46.0.5.25", {"center": v(15.16, 47.25) * mm, "radius": 1 * mm});
            skCircle(sketch, "E46.0.5.26", {"center": v(51.53, 47.25) * mm, "radius": 1 * mm});
            skCircle(sketch, "E46.0.5.29", {"center": v(78.8, 52.5) * mm, "radius": 1 * mm});
            skCircle(sketch, "E46.0.5.30", {"center": v(69.72, 57.75) * mm, "radius": 1 * mm});
            skCircle(sketch, "E46.0.5.32", {"center": v(-21.22, 47.25) * mm, "radius": 1 * mm});
            skCircle(sketch, "E46.0.5.33", {"center": v(-21.22, 57.75) * mm, "radius": 1 * mm});
            skCircle(sketch, "E46.0.5.34", {"center": v(6.06, 52.5) * mm, "radius": 1 * mm});
            skCircle(sketch, "E46.0.5.35", {"center": v(-12.12, 52.5) * mm, "radius": 1 * mm});
            skCircle(sketch, "E46.0.5.36", {"center": v(15.16, 57.75) * mm, "radius": 1 * mm});
            skCircle(sketch, "E46.0.5.37", {"center": v(-3.03, 57.75) * mm, "radius": 1 * mm});
            skPoint(sketch, "E46.0.6.1", {"position": v(0, 63) * mm});
            skCircle(sketch, "E46.0.6.6", {"center": v(-48.5, 63) * mm, "radius": 1 * mm});
            skCircle(sketch, "E46.0.6.7", {"center": v(-39.4, 57.75) * mm, "radius": 1 * mm});
            skCircle(sketch, "E46.0.6.8", {"center": v(51.53, 68.25) * mm, "radius": 1 * mm});
            skCircle(sketch, "E46.0.6.9", {"center": v(33.34, 57.75) * mm, "radius": 1 * mm});
            skCircle(sketch, "E46.0.6.10", {"center": v(42.44, 63) * mm, "radius": 1 * mm});
            skCircle(sketch, "E46.0.6.11", {"center": v(33.34, 68.25) * mm, "radius": 1 * mm});
            skCircle(sketch, "E46.0.6.12", {"center": v(24.25, 63) * mm, "radius": 1 * mm});
            skCircle(sketch, "E46.0.6.13", {"center": v(-57.6, 68.25) * mm, "radius": 1 * mm});
            skCircle(sketch, "E46.0.6.14", {"center": v(-75.78, 57.75) * mm, "radius": 1 * mm});
            skCircle(sketch, "E46.0.6.15", {"center": v(-39.4, 68.25) * mm, "radius": 1 * mm});
            skCircle(sketch, "E46.0.6.16", {"center": v(69.72, 57.75) * mm, "radius": 1 * mm});
            skCircle(sketch, "E46.0.6.18", {"center": v(60.62, 63) * mm, "radius": 1 * mm});
            skCircle(sketch, "E46.0.6.19", {"center": v(-66.68, 63) * mm, "radius": 1 * mm});
            skCircle(sketch, "E46.0.6.20", {"center": v(-30.31, 63) * mm, "radius": 1 * mm});
            skCircle(sketch, "E46.0.6.22", {"center": v(-57.6, 57.75) * mm, "radius": 1 * mm});
            skCircle(sketch, "E46.0.6.24", {"center": v(-3.03, 57.75) * mm, "radius": 1 * mm});
            skCircle(sketch, "E46.0.6.25", {"center": v(15.16, 57.75) * mm, "radius": 1 * mm});
            skCircle(sketch, "E46.0.6.26", {"center": v(51.53, 57.75) * mm, "radius": 1 * mm});
            skCircle(sketch, "E46.0.6.32", {"center": v(-21.22, 57.75) * mm, "radius": 1 * mm});
            skCircle(sketch, "E46.0.6.33", {"center": v(-21.22, 68.25) * mm, "radius": 1 * mm});
            skCircle(sketch, "E46.0.6.34", {"center": v(6.06, 63) * mm, "radius": 1 * mm});
            skCircle(sketch, "E46.0.6.35", {"center": v(-12.12, 63) * mm, "radius": 1 * mm});
            skCircle(sketch, "E46.0.6.36", {"center": v(15.16, 68.25) * mm, "radius": 1 * mm});
            skCircle(sketch, "E46.0.6.37", {"center": v(-3.03, 68.25) * mm, "radius": 1 * mm});
            skPoint(sketch, "E46.0.7.1", {"position": v(0, 73.5) * mm});
            skCircle(sketch, "E46.0.7.6", {"center": v(-48.5, 73.5) * mm, "radius": 1 * mm});
            skCircle(sketch, "E46.0.7.7", {"center": v(-39.4, 68.25) * mm, "radius": 1 * mm});
            skCircle(sketch, "E46.0.7.8", {"center": v(51.53, 78.75) * mm, "radius": 1 * mm});
            skCircle(sketch, "E46.0.7.9", {"center": v(33.34, 68.25) * mm, "radius": 1 * mm});
            skCircle(sketch, "E46.0.7.10", {"center": v(42.44, 73.5) * mm, "radius": 1 * mm});
            skCircle(sketch, "E46.0.7.11", {"center": v(33.34, 78.75) * mm, "radius": 1 * mm});
            skCircle(sketch, "E46.0.7.12", {"center": v(24.25, 73.5) * mm, "radius": 1 * mm});
            skCircle(sketch, "E46.0.7.13", {"center": v(-57.6, 78.75) * mm, "radius": 1 * mm});
            skCircle(sketch, "E46.0.7.15", {"center": v(-39.4, 78.75) * mm, "radius": 1 * mm});
            skCircle(sketch, "E46.0.7.18", {"center": v(60.62, 73.5) * mm, "radius": 1 * mm});
            skCircle(sketch, "E46.0.7.20", {"center": v(-30.31, 73.5) * mm, "radius": 1 * mm});
            skCircle(sketch, "E46.0.7.22", {"center": v(-57.6, 68.25) * mm, "radius": 1 * mm});
            skCircle(sketch, "E46.0.7.24", {"center": v(-3.03, 68.25) * mm, "radius": 1 * mm});
            skCircle(sketch, "E46.0.7.25", {"center": v(15.16, 68.25) * mm, "radius": 1 * mm});
            skCircle(sketch, "E46.0.7.26", {"center": v(51.53, 68.25) * mm, "radius": 1 * mm});
            skCircle(sketch, "E46.0.7.32", {"center": v(-21.22, 68.25) * mm, "radius": 1 * mm});
            skCircle(sketch, "E46.0.7.33", {"center": v(-21.22, 78.75) * mm, "radius": 1 * mm});
            skCircle(sketch, "E46.0.7.34", {"center": v(6.06, 73.5) * mm, "radius": 1 * mm});
            skCircle(sketch, "E46.0.7.35", {"center": v(-12.12, 73.5) * mm, "radius": 1 * mm});
            skCircle(sketch, "E46.0.7.36", {"center": v(15.16, 78.75) * mm, "radius": 1 * mm});
            skCircle(sketch, "E46.0.7.37", {"center": v(-3.03, 78.75) * mm, "radius": 1 * mm});
            skPoint(sketch, "E46.0.8.1", {"position": v(0, 84) * mm});
            skCircle(sketch, "E46.0.8.6", {"center": v(-48.5, 84) * mm, "radius": 1 * mm});
            skCircle(sketch, "E46.0.8.7", {"center": v(-39.4, 78.75) * mm, "radius": 1 * mm});
            skCircle(sketch, "E46.0.8.9", {"center": v(33.34, 78.75) * mm, "radius": 1 * mm});
            skCircle(sketch, "E46.0.8.10", {"center": v(42.44, 84) * mm, "radius": 1 * mm});
            skCircle(sketch, "E46.0.8.11", {"center": v(33.34, 89.25) * mm, "radius": 1 * mm});
            skCircle(sketch, "E46.0.8.12", {"center": v(24.25, 84) * mm, "radius": 1 * mm});
            skCircle(sketch, "E46.0.8.15", {"center": v(-39.4, 89.25) * mm, "radius": 1 * mm});
            skCircle(sketch, "E46.0.8.20", {"center": v(-30.31, 84) * mm, "radius": 1 * mm});
            skCircle(sketch, "E46.0.8.22", {"center": v(-57.6, 78.75) * mm, "radius": 1 * mm});
            skCircle(sketch, "E46.0.8.24", {"center": v(-3.03, 78.75) * mm, "radius": 1 * mm});
            skCircle(sketch, "E46.0.8.25", {"center": v(15.16, 78.75) * mm, "radius": 1 * mm});
            skCircle(sketch, "E46.0.8.26", {"center": v(51.53, 78.75) * mm, "radius": 1 * mm});
            skCircle(sketch, "E46.0.8.32", {"center": v(-21.22, 78.75) * mm, "radius": 1 * mm});
            skCircle(sketch, "E46.0.8.33", {"center": v(-21.22, 89.25) * mm, "radius": 1 * mm});
            skCircle(sketch, "E46.0.8.34", {"center": v(6.06, 84) * mm, "radius": 1 * mm});
            skCircle(sketch, "E46.0.8.35", {"center": v(-12.12, 84) * mm, "radius": 1 * mm});
            skCircle(sketch, "E46.0.8.36", {"center": v(15.16, 89.25) * mm, "radius": 1 * mm});
            skCircle(sketch, "E46.0.8.37", {"center": v(-3.03, 89.25) * mm, "radius": 1 * mm});
            skCircle(sketch, "E46.0.9.7", {"center": v(-39.4, 89.25) * mm, "radius": 1 * mm});
            skCircle(sketch, "E46.0.9.9", {"center": v(33.34, 89.25) * mm, "radius": 1 * mm});
            skCircle(sketch, "E46.0.9.24", {"center": v(-3.03, 89.25) * mm, "radius": 1 * mm});
            skCircle(sketch, "E46.0.9.25", {"center": v(15.16, 89.25) * mm, "radius": 1 * mm});
            skCircle(sketch, "E46.0.9.32", {"center": v(-21.22, 89.25) * mm, "radius": 1 * mm});
            skCircle(sketch, "E46.0.9.34", {"center": v(6.06, 94.5) * mm, "radius": 1 * mm});
            skCircle(sketch, "E46.0.9.35", {"center": v(-12.12, 94.5) * mm, "radius": 1 * mm});
            skPoint(sketch, "E47.0.1.0", {"position": v(0, -10.5) * mm});
            skCircle(sketch, "E47.0.1.1", {"center": v(33.34, -15.75) * mm, "radius": 1 * mm});
            skCircle(sketch, "E47.0.1.2", {"center": v(42.44, -10.5) * mm, "radius": 1 * mm});
            skCircle(sketch, "E47.0.1.3", {"center": v(15.16, -15.75) * mm, "radius": 1 * mm});
            skCircle(sketch, "E47.0.1.4", {"center": v(-3.03, -15.75) * mm, "radius": 1 * mm});
            skCircle(sketch, "E47.0.1.5", {"center": v(51.53, -15.75) * mm, "radius": 1 * mm});
            skCircle(sketch, "E47.0.1.6", {"center": v(60.62, -10.5) * mm, "radius": 1 * mm});
            skCircle(sketch, "E47.0.1.7", {"center": v(-48.5, -10.5) * mm, "radius": 1 * mm});
            skCircle(sketch, "E47.0.1.8", {"center": v(-39.4, -15.75) * mm, "radius": 1 * mm});
            skCircle(sketch, "E47.0.1.9", {"center": v(-30.31, -10.5) * mm, "radius": 1 * mm});
            skCircle(sketch, "E47.0.1.10", {"center": v(-21.22, -15.75) * mm, "radius": 1 * mm});
            skCircle(sketch, "E47.0.1.11", {"center": v(87.9, -15.75) * mm, "radius": 1 * mm});
            skCircle(sketch, "E47.0.1.12", {"center": v(78.8, -10.5) * mm, "radius": 1 * mm});
            skCircle(sketch, "E47.0.1.13", {"center": v(-93.96, -15.75) * mm, "radius": 1 * mm});
            skCircle(sketch, "E47.0.1.14", {"center": v(97, -10.5) * mm, "radius": 1 * mm});
            skCircle(sketch, "E47.0.1.15", {"center": v(-84.87, -10.5) * mm, "radius": 1 * mm});
            skCircle(sketch, "E47.0.1.16", {"center": v(-57.6, -15.75) * mm, "radius": 1 * mm});
            skCircle(sketch, "E47.0.1.17", {"center": v(-75.78, -15.75) * mm, "radius": 1 * mm});
            skCircle(sketch, "E47.0.1.18", {"center": v(-66.68, -10.5) * mm, "radius": 1 * mm});
            skCircle(sketch, "E47.0.1.19", {"center": v(69.72, -15.75) * mm, "radius": 1 * mm});
            skCircle(sketch, "E47.0.1.22", {"center": v(24.25, -10.5) * mm, "radius": 1 * mm});
            skCircle(sketch, "E47.0.1.23", {"center": v(6.06, -10.5) * mm, "radius": 1 * mm});
            skCircle(sketch, "E47.0.1.29", {"center": v(-12.12, -10.5) * mm, "radius": 1 * mm});
            skPoint(sketch, "E47.0.2.0", {"position": v(0, -21) * mm});
            skCircle(sketch, "E47.0.2.1", {"center": v(33.34, -26.25) * mm, "radius": 1 * mm});
            skCircle(sketch, "E47.0.2.2", {"center": v(42.44, -21) * mm, "radius": 1 * mm});
            skCircle(sketch, "E47.0.2.3", {"center": v(15.16, -26.25) * mm, "radius": 1 * mm});
            skCircle(sketch, "E47.0.2.4", {"center": v(-3.03, -26.25) * mm, "radius": 1 * mm});
            skCircle(sketch, "E47.0.2.5", {"center": v(51.53, -26.25) * mm, "radius": 1 * mm});
            skCircle(sketch, "E47.0.2.6", {"center": v(60.62, -21) * mm, "radius": 1 * mm});
            skCircle(sketch, "E47.0.2.7", {"center": v(-48.5, -21) * mm, "radius": 1 * mm});
            skCircle(sketch, "E47.0.2.8", {"center": v(-39.4, -26.25) * mm, "radius": 1 * mm});
            skCircle(sketch, "E47.0.2.9", {"center": v(-30.31, -21) * mm, "radius": 1 * mm});
            skCircle(sketch, "E47.0.2.10", {"center": v(-21.22, -26.25) * mm, "radius": 1 * mm});
            skCircle(sketch, "E47.0.2.11", {"center": v(87.9, -26.25) * mm, "radius": 1 * mm});
            skCircle(sketch, "E47.0.2.12", {"center": v(78.8, -21) * mm, "radius": 1 * mm});
            skCircle(sketch, "E47.0.2.15", {"center": v(-84.87, -21) * mm, "radius": 1 * mm});
            skCircle(sketch, "E47.0.2.16", {"center": v(-57.6, -26.25) * mm, "radius": 1 * mm});
            skCircle(sketch, "E47.0.2.17", {"center": v(-75.78, -26.25) * mm, "radius": 1 * mm});
            skCircle(sketch, "E47.0.2.18", {"center": v(-66.68, -21) * mm, "radius": 1 * mm});
            skCircle(sketch, "E47.0.2.19", {"center": v(69.72, -26.25) * mm, "radius": 1 * mm});
            skCircle(sketch, "E47.0.2.20", {"center": v(51.53, -15.75) * mm, "radius": 1 * mm});
            skCircle(sketch, "E47.0.2.21", {"center": v(33.34, -15.75) * mm, "radius": 1 * mm});
            skCircle(sketch, "E47.0.2.22", {"center": v(24.25, -21) * mm, "radius": 1 * mm});
            skCircle(sketch, "E47.0.2.23", {"center": v(6.06, -21) * mm, "radius": 1 * mm});
            skCircle(sketch, "E47.0.2.24", {"center": v(69.72, -15.75) * mm, "radius": 1 * mm});
            skCircle(sketch, "E47.0.2.25", {"center": v(-39.4, -15.75) * mm, "radius": 1 * mm});
            skCircle(sketch, "E47.0.2.26", {"center": v(-57.6, -15.75) * mm, "radius": 1 * mm});
            skCircle(sketch, "E47.0.2.27", {"center": v(87.9, -15.75) * mm, "radius": 1 * mm});
            skCircle(sketch, "E47.0.2.28", {"center": v(-21.22, -15.75) * mm, "radius": 1 * mm});
            skCircle(sketch, "E47.0.2.29", {"center": v(-12.12, -21) * mm, "radius": 1 * mm});
            skCircle(sketch, "E47.0.2.30", {"center": v(-93.96, -15.75) * mm, "radius": 1 * mm});
            skCircle(sketch, "E47.0.2.31", {"center": v(-75.78, -15.75) * mm, "radius": 1 * mm});
            skCircle(sketch, "E47.0.2.32", {"center": v(15.16, -15.75) * mm, "radius": 1 * mm});
            skCircle(sketch, "E47.0.2.33", {"center": v(-3.03, -15.75) * mm, "radius": 1 * mm});
            skCircle(sketch, "E47.0.2.34", {"center": v(-39.4, -15.75) * mm, "radius": 1 * mm});
            skCircle(sketch, "E47.0.2.35", {"center": v(69.72, -15.75) * mm, "radius": 1 * mm});
            skCircle(sketch, "E47.0.2.36", {"center": v(-21.22, -15.75) * mm, "radius": 1 * mm});
            skCircle(sketch, "E47.0.2.37", {"center": v(87.9, -15.75) * mm, "radius": 1 * mm});
            skCircle(sketch, "E47.0.2.38", {"center": v(51.53, -15.75) * mm, "radius": 1 * mm});
            skCircle(sketch, "E47.0.2.39", {"center": v(-57.6, -15.75) * mm, "radius": 1 * mm});
            skCircle(sketch, "E47.0.2.40", {"center": v(33.34, -15.75) * mm, "radius": 1 * mm});
            skCircle(sketch, "E47.0.2.41", {"center": v(-75.78, -15.75) * mm, "radius": 1 * mm});
            skCircle(sketch, "E47.0.2.42", {"center": v(-93.96, -15.75) * mm, "radius": 1 * mm});
            skCircle(sketch, "E47.0.2.43", {"center": v(15.16, -15.75) * mm, "radius": 1 * mm});
            skCircle(sketch, "E47.0.2.44", {"center": v(-3.03, -15.75) * mm, "radius": 1 * mm});
            skPoint(sketch, "E47.0.3.0", {"position": v(0, -31.5) * mm});
            skCircle(sketch, "E47.0.3.1", {"center": v(33.34, -36.75) * mm, "radius": 1 * mm});
            skCircle(sketch, "E47.0.3.2", {"center": v(42.44, -31.5) * mm, "radius": 1 * mm});
            skCircle(sketch, "E47.0.3.3", {"center": v(15.16, -36.75) * mm, "radius": 1 * mm});
            skCircle(sketch, "E47.0.3.4", {"center": v(-3.03, -36.75) * mm, "radius": 1 * mm});
            skCircle(sketch, "E47.0.3.5", {"center": v(51.53, -36.75) * mm, "radius": 1 * mm});
            skCircle(sketch, "E47.0.3.6", {"center": v(60.62, -31.5) * mm, "radius": 1 * mm});
            skCircle(sketch, "E47.0.3.7", {"center": v(-48.5, -31.5) * mm, "radius": 1 * mm});
            skCircle(sketch, "E47.0.3.8", {"center": v(-39.4, -36.75) * mm, "radius": 1 * mm});
            skCircle(sketch, "E47.0.3.9", {"center": v(-30.31, -31.5) * mm, "radius": 1 * mm});
            skCircle(sketch, "E47.0.3.10", {"center": v(-21.22, -36.75) * mm, "radius": 1 * mm});
            skCircle(sketch, "E47.0.3.11", {"center": v(87.9, -36.75) * mm, "radius": 1 * mm});
            skCircle(sketch, "E47.0.3.12", {"center": v(78.8, -31.5) * mm, "radius": 1 * mm});
            skCircle(sketch, "E47.0.3.15", {"center": v(-84.87, -31.5) * mm, "radius": 1 * mm});
            skCircle(sketch, "E47.0.3.16", {"center": v(-57.6, -36.75) * mm, "radius": 1 * mm});
            skCircle(sketch, "E47.0.3.17", {"center": v(-75.78, -36.75) * mm, "radius": 1 * mm});
            skCircle(sketch, "E47.0.3.18", {"center": v(-66.68, -31.5) * mm, "radius": 1 * mm});
            skCircle(sketch, "E47.0.3.19", {"center": v(69.72, -36.75) * mm, "radius": 1 * mm});
            skCircle(sketch, "E47.0.3.20", {"center": v(51.53, -26.25) * mm, "radius": 1 * mm});
            skCircle(sketch, "E47.0.3.21", {"center": v(33.34, -26.25) * mm, "radius": 1 * mm});
            skCircle(sketch, "E47.0.3.22", {"center": v(24.25, -31.5) * mm, "radius": 1 * mm});
            skCircle(sketch, "E47.0.3.23", {"center": v(6.06, -31.5) * mm, "radius": 1 * mm});
            skCircle(sketch, "E47.0.3.24", {"center": v(69.72, -26.25) * mm, "radius": 1 * mm});
            skCircle(sketch, "E47.0.3.25", {"center": v(-39.4, -26.25) * mm, "radius": 1 * mm});
            skCircle(sketch, "E47.0.3.26", {"center": v(-57.6, -26.25) * mm, "radius": 1 * mm});
            skCircle(sketch, "E47.0.3.27", {"center": v(87.9, -26.25) * mm, "radius": 1 * mm});
            skCircle(sketch, "E47.0.3.28", {"center": v(-21.22, -26.25) * mm, "radius": 1 * mm});
            skCircle(sketch, "E47.0.3.29", {"center": v(-12.12, -31.5) * mm, "radius": 1 * mm});
            skCircle(sketch, "E47.0.3.31", {"center": v(-75.78, -26.25) * mm, "radius": 1 * mm});
            skCircle(sketch, "E47.0.3.32", {"center": v(15.16, -26.25) * mm, "radius": 1 * mm});
            skCircle(sketch, "E47.0.3.33", {"center": v(-3.03, -26.25) * mm, "radius": 1 * mm});
            skCircle(sketch, "E47.0.3.34", {"center": v(-39.4, -26.25) * mm, "radius": 1 * mm});
            skCircle(sketch, "E47.0.3.35", {"center": v(69.72, -26.25) * mm, "radius": 1 * mm});
            skCircle(sketch, "E47.0.3.36", {"center": v(-21.22, -26.25) * mm, "radius": 1 * mm});
            skCircle(sketch, "E47.0.3.37", {"center": v(87.9, -26.25) * mm, "radius": 1 * mm});
            skCircle(sketch, "E47.0.3.38", {"center": v(51.53, -26.25) * mm, "radius": 1 * mm});
            skCircle(sketch, "E47.0.3.39", {"center": v(-57.6, -26.25) * mm, "radius": 1 * mm});
            skCircle(sketch, "E47.0.3.40", {"center": v(33.34, -26.25) * mm, "radius": 1 * mm});
            skCircle(sketch, "E47.0.3.41", {"center": v(-75.78, -26.25) * mm, "radius": 1 * mm});
            skCircle(sketch, "E47.0.3.43", {"center": v(15.16, -26.25) * mm, "radius": 1 * mm});
            skCircle(sketch, "E47.0.3.44", {"center": v(-3.03, -26.25) * mm, "radius": 1 * mm});
            skPoint(sketch, "E47.0.4.0", {"position": v(0, -42) * mm});
            skCircle(sketch, "E47.0.4.1", {"center": v(33.34, -47.25) * mm, "radius": 1 * mm});
            skCircle(sketch, "E47.0.4.2", {"center": v(42.44, -42) * mm, "radius": 1 * mm});
            skCircle(sketch, "E47.0.4.3", {"center": v(15.16, -47.25) * mm, "radius": 1 * mm});
            skCircle(sketch, "E47.0.4.4", {"center": v(-3.03, -47.25) * mm, "radius": 1 * mm});
            skCircle(sketch, "E47.0.4.5", {"center": v(51.53, -47.25) * mm, "radius": 1 * mm});
            skCircle(sketch, "E47.0.4.6", {"center": v(60.62, -42) * mm, "radius": 1 * mm});
            skCircle(sketch, "E47.0.4.7", {"center": v(-48.5, -42) * mm, "radius": 1 * mm});
            skCircle(sketch, "E47.0.4.8", {"center": v(-39.4, -47.25) * mm, "radius": 1 * mm});
            skCircle(sketch, "E47.0.4.9", {"center": v(-30.31, -42) * mm, "radius": 1 * mm});
            skCircle(sketch, "E47.0.4.10", {"center": v(-21.22, -47.25) * mm, "radius": 1 * mm});
            skCircle(sketch, "E47.0.4.12", {"center": v(78.8, -42) * mm, "radius": 1 * mm});
            skCircle(sketch, "E47.0.4.15", {"center": v(-84.87, -42) * mm, "radius": 1 * mm});
            skCircle(sketch, "E47.0.4.16", {"center": v(-57.6, -47.25) * mm, "radius": 1 * mm});
            skCircle(sketch, "E47.0.4.17", {"center": v(-75.78, -47.25) * mm, "radius": 1 * mm});
            skCircle(sketch, "E47.0.4.18", {"center": v(-66.68, -42) * mm, "radius": 1 * mm});
            skCircle(sketch, "E47.0.4.19", {"center": v(69.72, -47.25) * mm, "radius": 1 * mm});
            skCircle(sketch, "E47.0.4.20", {"center": v(51.53, -36.75) * mm, "radius": 1 * mm});
            skCircle(sketch, "E47.0.4.21", {"center": v(33.34, -36.75) * mm, "radius": 1 * mm});
            skCircle(sketch, "E47.0.4.22", {"center": v(24.25, -42) * mm, "radius": 1 * mm});
            skCircle(sketch, "E47.0.4.23", {"center": v(6.06, -42) * mm, "radius": 1 * mm});
            skCircle(sketch, "E47.0.4.24", {"center": v(69.72, -36.75) * mm, "radius": 1 * mm});
            skCircle(sketch, "E47.0.4.25", {"center": v(-39.4, -36.75) * mm, "radius": 1 * mm});
            skCircle(sketch, "E47.0.4.26", {"center": v(-57.6, -36.75) * mm, "radius": 1 * mm});
            skCircle(sketch, "E47.0.4.27", {"center": v(87.9, -36.75) * mm, "radius": 1 * mm});
            skCircle(sketch, "E47.0.4.28", {"center": v(-21.22, -36.75) * mm, "radius": 1 * mm});
            skCircle(sketch, "E47.0.4.29", {"center": v(-12.12, -42) * mm, "radius": 1 * mm});
            skCircle(sketch, "E47.0.4.31", {"center": v(-75.78, -36.75) * mm, "radius": 1 * mm});
            skCircle(sketch, "E47.0.4.32", {"center": v(15.16, -36.75) * mm, "radius": 1 * mm});
            skCircle(sketch, "E47.0.4.33", {"center": v(-3.03, -36.75) * mm, "radius": 1 * mm});
            skCircle(sketch, "E47.0.4.34", {"center": v(-39.4, -36.75) * mm, "radius": 1 * mm});
            skCircle(sketch, "E47.0.4.35", {"center": v(69.72, -36.75) * mm, "radius": 1 * mm});
            skCircle(sketch, "E47.0.4.36", {"center": v(-21.22, -36.75) * mm, "radius": 1 * mm});
            skCircle(sketch, "E47.0.4.37", {"center": v(87.9, -36.75) * mm, "radius": 1 * mm});
            skCircle(sketch, "E47.0.4.38", {"center": v(51.53, -36.75) * mm, "radius": 1 * mm});
            skCircle(sketch, "E47.0.4.39", {"center": v(-57.6, -36.75) * mm, "radius": 1 * mm});
            skCircle(sketch, "E47.0.4.40", {"center": v(33.34, -36.75) * mm, "radius": 1 * mm});
            skCircle(sketch, "E47.0.4.41", {"center": v(-75.78, -36.75) * mm, "radius": 1 * mm});
            skCircle(sketch, "E47.0.4.43", {"center": v(15.16, -36.75) * mm, "radius": 1 * mm});
            skCircle(sketch, "E47.0.4.44", {"center": v(-3.03, -36.75) * mm, "radius": 1 * mm});
            skPoint(sketch, "E47.0.5.0", {"position": v(0, -52.5) * mm});
            skCircle(sketch, "E47.0.5.1", {"center": v(33.34, -57.75) * mm, "radius": 1 * mm});
            skCircle(sketch, "E47.0.5.2", {"center": v(42.44, -52.5) * mm, "radius": 1 * mm});
            skCircle(sketch, "E47.0.5.3", {"center": v(15.16, -57.75) * mm, "radius": 1 * mm});
            skCircle(sketch, "E47.0.5.4", {"center": v(-3.03, -57.75) * mm, "radius": 1 * mm});
            skCircle(sketch, "E47.0.5.5", {"center": v(51.53, -57.75) * mm, "radius": 1 * mm});
            skCircle(sketch, "E47.0.5.6", {"center": v(60.62, -52.5) * mm, "radius": 1 * mm});
            skCircle(sketch, "E47.0.5.7", {"center": v(-48.5, -52.5) * mm, "radius": 1 * mm});
            skCircle(sketch, "E47.0.5.8", {"center": v(-39.4, -57.75) * mm, "radius": 1 * mm});
            skCircle(sketch, "E47.0.5.9", {"center": v(-30.31, -52.5) * mm, "radius": 1 * mm});
            skCircle(sketch, "E47.0.5.10", {"center": v(-21.22, -57.75) * mm, "radius": 1 * mm});
            skCircle(sketch, "E47.0.5.12", {"center": v(78.8, -52.5) * mm, "radius": 1 * mm});
            skCircle(sketch, "E47.0.5.16", {"center": v(-57.6, -57.75) * mm, "radius": 1 * mm});
            skCircle(sketch, "E47.0.5.17", {"center": v(-75.78, -57.75) * mm, "radius": 1 * mm});
            skCircle(sketch, "E47.0.5.18", {"center": v(-66.68, -52.5) * mm, "radius": 1 * mm});
            skCircle(sketch, "E47.0.5.19", {"center": v(69.72, -57.75) * mm, "radius": 1 * mm});
            skCircle(sketch, "E47.0.5.20", {"center": v(51.53, -47.25) * mm, "radius": 1 * mm});
            skCircle(sketch, "E47.0.5.21", {"center": v(33.34, -47.25) * mm, "radius": 1 * mm});
            skCircle(sketch, "E47.0.5.22", {"center": v(24.25, -52.5) * mm, "radius": 1 * mm});
            skCircle(sketch, "E47.0.5.23", {"center": v(6.06, -52.5) * mm, "radius": 1 * mm});
            skCircle(sketch, "E47.0.5.24", {"center": v(69.72, -47.25) * mm, "radius": 1 * mm});
            skCircle(sketch, "E47.0.5.25", {"center": v(-39.4, -47.25) * mm, "radius": 1 * mm});
            skCircle(sketch, "E47.0.5.26", {"center": v(-57.6, -47.25) * mm, "radius": 1 * mm});
            skCircle(sketch, "E47.0.5.28", {"center": v(-21.22, -47.25) * mm, "radius": 1 * mm});
            skCircle(sketch, "E47.0.5.29", {"center": v(-12.12, -52.5) * mm, "radius": 1 * mm});
            skCircle(sketch, "E47.0.5.31", {"center": v(-75.78, -47.25) * mm, "radius": 1 * mm});
            skCircle(sketch, "E47.0.5.32", {"center": v(15.16, -47.25) * mm, "radius": 1 * mm});
            skCircle(sketch, "E47.0.5.33", {"center": v(-3.03, -47.25) * mm, "radius": 1 * mm});
            skCircle(sketch, "E47.0.5.34", {"center": v(-39.4, -47.25) * mm, "radius": 1 * mm});
            skCircle(sketch, "E47.0.5.35", {"center": v(69.72, -47.25) * mm, "radius": 1 * mm});
            skCircle(sketch, "E47.0.5.36", {"center": v(-21.22, -47.25) * mm, "radius": 1 * mm});
            skCircle(sketch, "E47.0.5.38", {"center": v(51.53, -47.25) * mm, "radius": 1 * mm});
            skCircle(sketch, "E47.0.5.39", {"center": v(-57.6, -47.25) * mm, "radius": 1 * mm});
            skCircle(sketch, "E47.0.5.40", {"center": v(33.34, -47.25) * mm, "radius": 1 * mm});
            skCircle(sketch, "E47.0.5.41", {"center": v(-75.78, -47.25) * mm, "radius": 1 * mm});
            skCircle(sketch, "E47.0.5.43", {"center": v(15.16, -47.25) * mm, "radius": 1 * mm});
            skCircle(sketch, "E47.0.5.44", {"center": v(-3.03, -47.25) * mm, "radius": 1 * mm});
            skPoint(sketch, "E47.0.6.0", {"position": v(0, -63) * mm});
            skCircle(sketch, "E47.0.6.1", {"center": v(33.34, -68.25) * mm, "radius": 1 * mm});
            skCircle(sketch, "E47.0.6.2", {"center": v(42.44, -63) * mm, "radius": 1 * mm});
            skCircle(sketch, "E47.0.6.3", {"center": v(15.16, -68.25) * mm, "radius": 1 * mm});
            skCircle(sketch, "E47.0.6.4", {"center": v(-3.03, -68.25) * mm, "radius": 1 * mm});
            skCircle(sketch, "E47.0.6.5", {"center": v(51.53, -68.25) * mm, "radius": 1 * mm});
            skCircle(sketch, "E47.0.6.6", {"center": v(60.62, -63) * mm, "radius": 1 * mm});
            skCircle(sketch, "E47.0.6.7", {"center": v(-48.5, -63) * mm, "radius": 1 * mm});
            skCircle(sketch, "E47.0.6.8", {"center": v(-39.4, -68.25) * mm, "radius": 1 * mm});
            skCircle(sketch, "E47.0.6.9", {"center": v(-30.31, -63) * mm, "radius": 1 * mm});
            skCircle(sketch, "E47.0.6.10", {"center": v(-21.22, -68.25) * mm, "radius": 1 * mm});
            skCircle(sketch, "E47.0.6.16", {"center": v(-57.6, -68.25) * mm, "radius": 1 * mm});
            skCircle(sketch, "E47.0.6.18", {"center": v(-66.68, -63) * mm, "radius": 1 * mm});
            skCircle(sketch, "E47.0.6.20", {"center": v(51.53, -57.75) * mm, "radius": 1 * mm});
            skCircle(sketch, "E47.0.6.21", {"center": v(33.34, -57.75) * mm, "radius": 1 * mm});
            skCircle(sketch, "E47.0.6.22", {"center": v(24.25, -63) * mm, "radius": 1 * mm});
            skCircle(sketch, "E47.0.6.23", {"center": v(6.06, -63) * mm, "radius": 1 * mm});
            skCircle(sketch, "E47.0.6.24", {"center": v(69.72, -57.75) * mm, "radius": 1 * mm});
            skCircle(sketch, "E47.0.6.25", {"center": v(-39.4, -57.75) * mm, "radius": 1 * mm});
            skCircle(sketch, "E47.0.6.26", {"center": v(-57.6, -57.75) * mm, "radius": 1 * mm});
            skCircle(sketch, "E47.0.6.28", {"center": v(-21.22, -57.75) * mm, "radius": 1 * mm});
            skCircle(sketch, "E47.0.6.29", {"center": v(-12.12, -63) * mm, "radius": 1 * mm});
            skCircle(sketch, "E47.0.6.31", {"center": v(-75.78, -57.75) * mm, "radius": 1 * mm});
            skCircle(sketch, "E47.0.6.32", {"center": v(15.16, -57.75) * mm, "radius": 1 * mm});
            skCircle(sketch, "E47.0.6.33", {"center": v(-3.03, -57.75) * mm, "radius": 1 * mm});
            skCircle(sketch, "E47.0.6.34", {"center": v(-39.4, -57.75) * mm, "radius": 1 * mm});
            skCircle(sketch, "E47.0.6.35", {"center": v(69.72, -57.75) * mm, "radius": 1 * mm});
            skCircle(sketch, "E47.0.6.36", {"center": v(-21.22, -57.75) * mm, "radius": 1 * mm});
            skCircle(sketch, "E47.0.6.38", {"center": v(51.53, -57.75) * mm, "radius": 1 * mm});
            skCircle(sketch, "E47.0.6.39", {"center": v(-57.6, -57.75) * mm, "radius": 1 * mm});
            skCircle(sketch, "E47.0.6.40", {"center": v(33.34, -57.75) * mm, "radius": 1 * mm});
            skCircle(sketch, "E47.0.6.41", {"center": v(-75.78, -57.75) * mm, "radius": 1 * mm});
            skCircle(sketch, "E47.0.6.43", {"center": v(15.16, -57.75) * mm, "radius": 1 * mm});
            skCircle(sketch, "E47.0.6.44", {"center": v(-3.03, -57.75) * mm, "radius": 1 * mm});
            skPoint(sketch, "E47.0.7.0", {"position": v(0, -73.5) * mm});
            skCircle(sketch, "E47.0.7.1", {"center": v(33.34, -78.75) * mm, "radius": 1 * mm});
            skCircle(sketch, "E47.0.7.2", {"center": v(42.44, -73.5) * mm, "radius": 1 * mm});
            skCircle(sketch, "E47.0.7.3", {"center": v(15.16, -78.75) * mm, "radius": 1 * mm});
            skCircle(sketch, "E47.0.7.4", {"center": v(-3.03, -78.75) * mm, "radius": 1 * mm});
            skCircle(sketch, "E47.0.7.5", {"center": v(51.53, -78.75) * mm, "radius": 1 * mm});
            skCircle(sketch, "E47.0.7.6", {"center": v(60.62, -73.5) * mm, "radius": 1 * mm});
            skCircle(sketch, "E47.0.7.7", {"center": v(-48.5, -73.5) * mm, "radius": 1 * mm});
            skCircle(sketch, "E47.0.7.8", {"center": v(-39.4, -78.75) * mm, "radius": 1 * mm});
            skCircle(sketch, "E47.0.7.9", {"center": v(-30.31, -73.5) * mm, "radius": 1 * mm});
            skCircle(sketch, "E47.0.7.10", {"center": v(-21.22, -78.75) * mm, "radius": 1 * mm});
            skCircle(sketch, "E47.0.7.20", {"center": v(51.53, -68.25) * mm, "radius": 1 * mm});
            skCircle(sketch, "E47.0.7.21", {"center": v(33.34, -68.25) * mm, "radius": 1 * mm});
            skCircle(sketch, "E47.0.7.22", {"center": v(24.25, -73.5) * mm, "radius": 1 * mm});
            skCircle(sketch, "E47.0.7.23", {"center": v(6.06, -73.5) * mm, "radius": 1 * mm});
            skCircle(sketch, "E47.0.7.25", {"center": v(-39.4, -68.25) * mm, "radius": 1 * mm});
            skCircle(sketch, "E47.0.7.26", {"center": v(-57.6, -68.25) * mm, "radius": 1 * mm});
            skCircle(sketch, "E47.0.7.28", {"center": v(-21.22, -68.25) * mm, "radius": 1 * mm});
            skCircle(sketch, "E47.0.7.29", {"center": v(-12.12, -73.5) * mm, "radius": 1 * mm});
            skCircle(sketch, "E47.0.7.33", {"center": v(-3.03, -68.25) * mm, "radius": 1 * mm});
            skCircle(sketch, "E47.0.7.34", {"center": v(-39.4, -68.25) * mm, "radius": 1 * mm});
            skCircle(sketch, "E47.0.7.36", {"center": v(-21.22, -68.25) * mm, "radius": 1 * mm});
            skCircle(sketch, "E47.0.7.38", {"center": v(51.53, -68.25) * mm, "radius": 1 * mm});
            skCircle(sketch, "E47.0.7.39", {"center": v(-57.6, -68.25) * mm, "radius": 1 * mm});
            skCircle(sketch, "E47.0.7.40", {"center": v(33.34, -68.25) * mm, "radius": 1 * mm});
            skCircle(sketch, "E47.0.7.44", {"center": v(-3.03, -68.25) * mm, "radius": 1 * mm});
            skPoint(sketch, "E47.0.8.0", {"position": v(0, -84) * mm});
            skCircle(sketch, "E47.0.8.1", {"center": v(33.34, -89.25) * mm, "radius": 1 * mm});
            skCircle(sketch, "E47.0.8.2", {"center": v(42.44, -84) * mm, "radius": 1 * mm});
            skCircle(sketch, "E47.0.8.3", {"center": v(15.16, -89.25) * mm, "radius": 1 * mm});
            skCircle(sketch, "E47.0.8.4", {"center": v(-3.03, -89.25) * mm, "radius": 1 * mm});
            skCircle(sketch, "E47.0.8.7", {"center": v(-48.5, -84) * mm, "radius": 1 * mm});
            skCircle(sketch, "E47.0.8.8", {"center": v(-39.4, -89.25) * mm, "radius": 1 * mm});
            skCircle(sketch, "E47.0.8.9", {"center": v(-30.31, -84) * mm, "radius": 1 * mm});
            skCircle(sketch, "E47.0.8.10", {"center": v(-21.22, -89.25) * mm, "radius": 1 * mm});
            skCircle(sketch, "E47.0.8.22", {"center": v(24.25, -84) * mm, "radius": 1 * mm});
            skCircle(sketch, "E47.0.8.25", {"center": v(-39.4, -78.75) * mm, "radius": 1 * mm});
            skCircle(sketch, "E47.0.8.26", {"center": v(-57.6, -78.75) * mm, "radius": 1 * mm});
            skCircle(sketch, "E47.0.8.28", {"center": v(-21.22, -78.75) * mm, "radius": 1 * mm});
            skCircle(sketch, "E47.0.8.29", {"center": v(-12.12, -84) * mm, "radius": 1 * mm});
            skCircle(sketch, "E47.0.8.32", {"center": v(15.16, -78.75) * mm, "radius": 1 * mm});
            skCircle(sketch, "E47.0.8.33", {"center": v(-3.03, -78.75) * mm, "radius": 1 * mm});
            skCircle(sketch, "E47.0.8.34", {"center": v(-39.4, -78.75) * mm, "radius": 1 * mm});
            skCircle(sketch, "E47.0.8.36", {"center": v(-21.22, -78.75) * mm, "radius": 1 * mm});
            skCircle(sketch, "E47.0.8.39", {"center": v(-57.6, -78.75) * mm, "radius": 1 * mm});
            skCircle(sketch, "E47.0.8.40", {"center": v(33.34, -78.75) * mm, "radius": 1 * mm});
            skCircle(sketch, "E47.0.8.43", {"center": v(15.16, -78.75) * mm, "radius": 1 * mm});
            skCircle(sketch, "E47.0.8.44", {"center": v(-3.03, -78.75) * mm, "radius": 1 * mm});
            skCircle(sketch, "E47.0.9.21", {"center": v(33.34, -89.25) * mm, "radius": 1 * mm});
            skCircle(sketch, "E47.0.9.23", {"center": v(6.06, -94.5) * mm, "radius": 1 * mm});
            skCircle(sketch, "E47.0.9.28", {"center": v(-21.22, -89.25) * mm, "radius": 1 * mm});
            skCircle(sketch, "E47.0.9.32", {"center": v(15.16, -89.25) * mm, "radius": 1 * mm});
            skCircle(sketch, "E47.0.9.33", {"center": v(-3.03, -89.25) * mm, "radius": 1 * mm});
            skCircle(sketch, "E47.0.9.34", {"center": v(-39.4, -89.25) * mm, "radius": 1 * mm});
            skCircle(sketch, "E47.0.9.36", {"center": v(-21.22, -89.25) * mm, "radius": 1 * mm});
            skCircle(sketch, "E47.0.9.40", {"center": v(33.34, -89.25) * mm, "radius": 1 * mm});
            skCircle(sketch, "E47.0.9.44", {"center": v(-3.03, -89.25) * mm, "radius": 1 * mm});
            skSolve(sketch);
        }
        {
            var Q0;
            Q0=qSketchRegion(id+"F2",true);
            extrude(context, id + "F4", {"entities" : qUnion([Q0]), "operationType" : NewBodyOperationType.REMOVE, "oppositeDirection" : true, "depth" : 3.17 * mm});
        }
        {
            var Q0;
            Q0=qSketchRegion(id+"F3",true);
            extrude(context, id + "F5", {"entities" : qUnion([Q0]), "operationType" : NewBodyOperationType.REMOVE, "endBound" : BoundingType.THROUGH_ALL, "oppositeDirection" : true, "depth" : 25 * mm});
        }
    });
